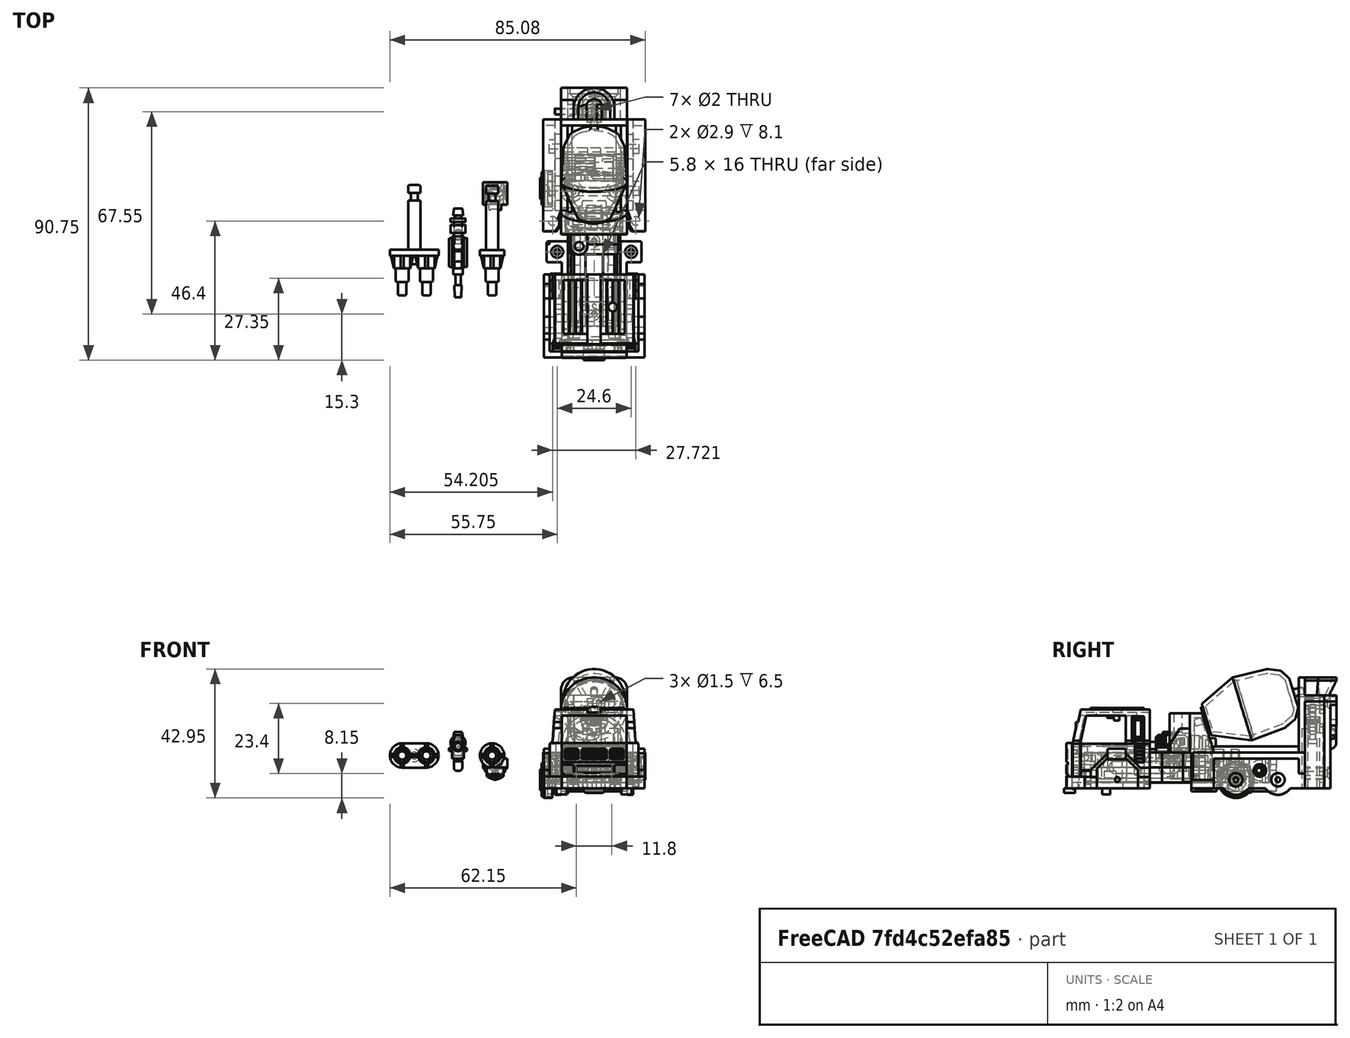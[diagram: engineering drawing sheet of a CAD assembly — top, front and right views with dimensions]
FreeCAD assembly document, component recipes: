
FREECAD ASSEMBLY — COMPONENT RECIPES ("MixMaster")

This assembly document has 25 components, labeled P0..P24 below (a component is one placed body or linked part). 24 of them carry a construction recipe — the FreeCAD feature program that regenerates the part from scratch, quoted from this document or its linked companion documents; the rest are supplied as boundary geometry only. No exploded tour is included for this assembly.
NOTE — document 3 of 4 of this assembly tour. The two overview renders and the header above are repeated from document 1; the component sections below continue where the previous document stopped.
COMPONENT P11 — recipe-attached ("Left_Wheel Holder", modeled in this document).
Construction recipe (the document's own serialized feature program — sketch geometry with constraints, then the solid features built on it; lengths are millimeters unless a unit is written):

FEATURE [PartDesign::SubShapeBinder] Binder013
  BindCopyOnChange = 0
  BindMode = 2
  ClaimChildren = false
  Context = -> Body021 [Binder013.]
  Fuse = false
  MakeFace = true
  OffsetFill = false
  OffsetIntersection = false
  OffsetJoinType = 0
  OffsetOpenResult = false
  PartialLoad = false
  Refine = true
  Relative = true
  _Version = 2
FEATURE [Sketcher::SketchObject] Sketch216
  ArcFitTolerance = 1e-06
  AttachmentSupport = -> [Binder013]
  ExternalGeometry = -> [Binder013]
  FullyConstrained = true
  MakeInternals = false
  MapMode = 5
  Placement = pos=(0.2,0,1.9e-15) rot=(0.57735,-0.57735,-0.57735;2.0944rad)
  sketch-geometry (6):
    g0: LineSegment StartX=77.35 StartY=0.7 StartZ=0 EndX=56.15 EndY=0.7 EndZ=0
    g1: LineSegment StartX=56.15 StartY=0.7 StartZ=0 EndX=56.15 EndY=-11 EndZ=0
    g2: LineSegment StartX=56.15 StartY=-11 StartZ=0 EndX=73.85 EndY=-11 EndZ=0
    g3: LineSegment StartX=73.85 StartY=-11 StartZ=0 EndX=73.85 EndY=-3.1 EndZ=0
    g4: LineSegment StartX=73.85 StartY=-3.1 StartZ=0 EndX=77.35 EndY=-3.1 EndZ=0
    g5: LineSegment StartX=77.35 StartY=-3.1 StartZ=0 EndX=77.35 EndY=0.7 EndZ=0
  constraints (18):
    c: Horizontal(g0)
    c: Coincident(g1,g0)
    c: Vertical(g1)
    c: Coincident(g2,g1)
    c: PointOnObject(g2,g-4)
    c: Horizontal(g2)
    c: Coincident(g3,g2)
    c: Vertical(g3)
    c: Coincident(g4,g3)
    c: Horizontal(g4)
    c: Coincident(g5,g4)
    c: Coincident(g5,g0)
    c: Vertical(g5)
    c: DistanceY(g1,g1) = 11.7
    c: DistanceY(g5,g5) = 3.8
    c: DistanceX(g4,g4) = 3.5
    c: DistanceX(g0,g0) = 21.2
    c: DistanceX(g4,g-4) = 1.7
FEATURE [PartDesign::Pad] Pad154
  Direction = (-1,0,-9.3e-15)
  Length = 2
  Length2 = 10
  Profile = -> Sketch216
  ReferenceAxis = -> Sketch216 [N_Axis]
  Refine = true
  Suppressed = false
  Type = 0
FEATURE [Sketcher::SketchObject] Sketch217
  ArcFitTolerance = 1e-06
  AttachmentSupport = -> [Pad154]
  ExternalGeometry = -> [Pad154]
  FullyConstrained = true
  MakeInternals = false
  MapMode = 5
  Placement = pos=(-1.8,0,-1.68e-14) rot=(0.57735,-0.57735,-0.57735;2.0944rad)
  sketch-geometry (12):
    g0: LineSegment StartX=62.15 StartY=0.7 StartZ=0 EndX=62.15 EndY=-1.3 EndZ=0
    g1: LineSegment StartX=62.15 StartY=-1.3 StartZ=0 EndX=68.25 EndY=-1.3 EndZ=0
    g2: LineSegment StartX=68.25 StartY=-1.3 StartZ=0 EndX=68.25 EndY=0.7 EndZ=0
    g3: LineSegment StartX=68.25 StartY=0.7 StartZ=0 EndX=62.15 EndY=0.7 EndZ=0
    g4: LineSegment StartX=73.85 StartY=-11 StartZ=0 EndX=73.85 EndY=-7.1 EndZ=0
    g5: LineSegment StartX=73.85 StartY=-7.1 StartZ=0 EndX=71.85 EndY=-7.1 EndZ=0
    g6: LineSegment StartX=71.85 StartY=-7.1 StartZ=0 EndX=71.85 EndY=-11 EndZ=0
    g7: LineSegment StartX=71.85 StartY=-11 StartZ=0 EndX=73.85 EndY=-11 EndZ=0
    g8: LineSegment StartX=56.15 StartY=-11 StartZ=0 EndX=58.15 EndY=-11 EndZ=0
    g9: LineSegment StartX=58.15 StartY=-11 StartZ=0 EndX=58.15 EndY=-7.1 EndZ=0
    g10: LineSegment StartX=58.15 StartY=-7.1 StartZ=0 EndX=56.15 EndY=-7.1 EndZ=0
    g11: LineSegment StartX=56.15 StartY=-7.1 StartZ=0 EndX=56.15 EndY=-11 EndZ=0
  constraints (34):
    c: Coincident(g0,g1)
    c: Coincident(g1,g2)
    c: Coincident(g2,g3)
    c: Coincident(g3,g0)
    c: Vertical(g0)
    c: Vertical(g2)
    c: Horizontal(g1)
    c: Horizontal(g3)
    c: PointOnObject(g0,g-5)
    c: Coincident(g4,g5)
    c: Coincident(g5,g6)
    c: Coincident(g6,g7)
    c: Coincident(g7,g4)
    c: Vertical(g4)
    c: Vertical(g6)
    c: Horizontal(g5)
    c: Horizontal(g7)
    c: Coincident(g4,g-6)
    c: Coincident(g8,g9)
    c: Coincident(g9,g10)
    c: Coincident(g10,g11)
    c: Coincident(g11,g8)
    c: Horizontal(g8)
    c: Horizontal(g10)
    c: Vertical(g9)
    c: Vertical(g11)
    c: Coincident(g8,g-6)
    c: DistanceX(g10,g10) = 2
    c: DistanceX(g5,g5) = 2
    c: DistanceY(g2,g2) = 2
    c: DistanceY(g9,g9) = 3.9
    c: DistanceY(g6,g6) = 3.9
    c: DistanceX(g1,g1) = 6.1
    c: DistanceX(g-5,g0) = 6
FEATURE [PartDesign::Pad] Pad155
  BaseFeature = -> Pad154
  Direction = (-1,0,-9.3e-15)
  Length = 2
  Length2 = 10
  Profile = -> Sketch217
  ReferenceAxis = -> Sketch217 [N_Axis]
  Refine = true
  Suppressed = false
  Type = 0
FEATURE [Sketcher::SketchObject] Sketch218
  ArcFitTolerance = 1e-06
  AttachmentSupport = -> [Pad155]
  ExternalGeometry = -> [Pad155]
  FullyConstrained = true
  MakeInternals = false
  MapMode = 5
  Placement = pos=(-3.8,0,-3.54e-14) rot=(0.57735,-0.57735,-0.57735;2.0944rad)
  sketch-geometry (12):
    g0: LineSegment StartX=58.15 StartY=-7.1 StartZ=0 EndX=54.15 EndY=-7.1 EndZ=0
    g1: LineSegment StartX=54.15 StartY=-7.1 StartZ=0 EndX=54.15 EndY=-11 EndZ=0
    g2: LineSegment StartX=54.15 StartY=-11 StartZ=0 EndX=58.15 EndY=-11 EndZ=0
    g3: LineSegment StartX=58.15 StartY=-11 StartZ=0 EndX=58.15 EndY=-7.1 EndZ=0
    g4: LineSegment StartX=71.85 StartY=-7.1 StartZ=0 EndX=71.85 EndY=-11 EndZ=0
    g5: LineSegment StartX=71.85 StartY=-11 StartZ=0 EndX=75.85 EndY=-11 EndZ=0
    g6: LineSegment StartX=75.85 StartY=-11 StartZ=0 EndX=75.85 EndY=-7.1 EndZ=0
    g7: LineSegment StartX=75.85 StartY=-7.1 StartZ=0 EndX=71.85 EndY=-7.1 EndZ=0
    g8: LineSegment StartX=68.25 StartY=-1.3 StartZ=0 EndX=68.25 EndY=2.2 EndZ=0
    g9: LineSegment StartX=68.25 StartY=2.2 StartZ=0 EndX=62.15 EndY=2.2 EndZ=0
    g10: LineSegment StartX=62.15 StartY=2.2 StartZ=0 EndX=62.15 EndY=-1.3 EndZ=0
    g11: LineSegment StartX=62.15 StartY=-1.3 StartZ=0 EndX=68.25 EndY=-1.3 EndZ=0
  constraints (31):
    c: Coincident(g0,g1)
    c: Coincident(g1,g2)
    c: Coincident(g2,g3)
    c: Coincident(g3,g0)
    c: Horizontal(g0)
    c: Horizontal(g2)
    c: Vertical(g1)
    c: Coincident(g0,g-7)
    c: Coincident(g4,g5)
    c: Coincident(g5,g6)
    c: Coincident(g6,g7)
    c: Coincident(g7,g4)
    c: Vertical(g6)
    c: Horizontal(g5)
    c: Horizontal(g7)
    c: Coincident(g4,g-10)
    c: Coincident(g8,g9)
    c: Coincident(g9,g10)
    c: Coincident(g10,g11)
    c: Coincident(g11,g8)
    c: Vertical(g8)
    c: Vertical(g10)
    c: Horizontal(g9)
    c: Horizontal(g11)
    c: Coincident(g8,g-4)
    c: PointOnObject(g-5,g10)
    c: Coincident(g-11,g4)
    c: Coincident(g2,g-8)
    c: DistanceX(g0,g0) = 4
    c: DistanceX(g7,g7) = 4
    c: DistanceY(g8,g8) = 3.5
FEATURE [PartDesign::Pad] Pad156
  BaseFeature = -> Pad155
  Direction = (-1,0,-9.3e-15)
  Length = 2
  Length2 = 10
  Profile = -> Sketch218
  ReferenceAxis = -> Sketch218 [N_Axis]
  Refine = true
  Suppressed = false
  Type = 0
FEATURE [Sketcher::SketchObject] Sketch219
  ArcFitTolerance = 1e-06
  AttachmentSupport = -> [Pad156]
  ExternalGeometry = -> [Pad156]
  FullyConstrained = true
  MakeInternals = false
  MapMode = 5
  Placement = pos=(-1.8,0,-1.68e-14) rot=(0.57735,-0.57735,-0.57735;2.0944rad)
  sketch-geometry (1):
    g0: Circle CenterX=65 CenterY=-8 CenterZ=0 NormalX=0 NormalY=0 NormalZ=1 AngleXU=0 Radius=0.75
  constraints (4):
    c: DistanceX(g-3,g-3) = 13.7
    c: Diameter(g0) = 1.5
    c: DistanceX(g-3,g0) = 6.85
    c: DistanceY(g-3,g0) = 3
FEATURE [PartDesign::Pocket] Pocket206
  BaseFeature = -> Pad156
  Direction = (1,0,9.3e-15)
  Length = 2
  Length2 = 5
  Profile = -> Sketch219
  ReferenceAxis = -> Sketch219 [N_Axis]
  Refine = true
  Suppressed = false
  Type = 0
FEATURE [Sketcher::SketchObject] Sketch220
  ArcFitTolerance = 1e-06
  AttachmentSupport = -> [Pocket206]
  ExternalGeometry = -> [Pocket206]
  FullyConstrained = true
  MakeInternals = false
  MapMode = 5
  Placement = pos=(-3.8,0,-3.54e-14) rot=(0.57735,0.57735,0.57735;2.0944rad)
  sketch-geometry (8):
    g0: LineSegment StartX=-75.85 StartY=-8.55 StartZ=0 EndX=-75.85 EndY=-9.55 EndZ=0
    g1: LineSegment StartX=-75.85 StartY=-9.55 StartZ=0 EndX=-73.85 EndY=-9.55 EndZ=0
    g2: LineSegment StartX=-73.85 StartY=-9.55 StartZ=0 EndX=-73.85 EndY=-8.55 EndZ=0
    g3: LineSegment StartX=-73.85 StartY=-8.55 StartZ=0 EndX=-75.85 EndY=-8.55 EndZ=0
    g4: LineSegment StartX=-54.15 StartY=-8.55 StartZ=0 EndX=-56.15 EndY=-8.55 EndZ=0
    g5: LineSegment StartX=-56.15 StartY=-8.55 StartZ=0 EndX=-56.15 EndY=-9.55 EndZ=0
    g6: LineSegment StartX=-56.15 StartY=-9.55 StartZ=0 EndX=-54.15 EndY=-9.55 EndZ=0
    g7: LineSegment StartX=-54.15 StartY=-9.55 StartZ=0 EndX=-54.15 EndY=-8.55 EndZ=0
  constraints (25):
    c: Coincident(g0,g1)
    c: Coincident(g1,g2)
    c: Coincident(g2,g3)
    c: Coincident(g3,g0)
    c: Vertical(g0)
    c: Vertical(g2)
    c: Horizontal(g1)
    c: Horizontal(g3)
    c: PointOnObject(g0,g-10)
    c: PointOnObject(g1,g-8)
    c: Coincident(g4,g5)
    c: Coincident(g5,g6)
    c: Coincident(g6,g7)
    c: Coincident(g7,g4)
    c: Horizontal(g4)
    c: Horizontal(g6)
    c: Vertical(g5)
    c: Vertical(g7)
    c: PointOnObject(g4,g-4)
    c: PointOnObject(g5,g-3)
    c: DistanceY(g7,g7) = 1
    c: DistanceY(g0,g0) = 1
    c: DistanceY(g-10,g-10) = 3.9
    c: DistanceY(g0,g-10) = 1.45
    c: DistanceY(g4,g-5) = 1.45
FEATURE [PartDesign::Pad] Pad157
  BaseFeature = -> Pocket206
  Direction = (1,0,9.3e-15)
  Length = 0.25
  Length2 = 10
  Profile = -> Sketch220
  ReferenceAxis = -> Sketch220 [N_Axis]
  Refine = true
  Suppressed = false
  Type = 0
FEATURE [PartDesign::Fillet] Fillet014
  Base = -> Pad157 [Edge76,Edge78,Edge85,Edge86]
  BaseFeature = -> Pad157
  Radius = 0.24
  Refine = true
  SupportTransform = false
  Suppressed = false
  UseAllEdges = false
FEATURE [Sketcher::SketchObject] Sketch221
  ArcFitTolerance = 1e-06
  AttachmentSupport = -> [Fillet014]
  ExternalGeometry = -> [Fillet014]
  FullyConstrained = true
  MakeInternals = false
  MapMode = 5
  Placement = pos=(0.2,0,1.9e-15) rot=(0.57735,0.57735,0.57735;2.0944rad)
  sketch-geometry (2):
    g0: Circle CenterX=-58.32 CenterY=-5.4 CenterZ=0 NormalX=0 NormalY=0 NormalZ=1 AngleXU=0 Radius=1.1
    g1: Circle CenterX=-75.55 CenterY=-0.67 CenterZ=0 NormalX=0 NormalY=0 NormalZ=1 AngleXU=0 Radius=1
  constraints (7):
    c: Diameter(g1) = 2
    c: Diameter(g0) = 2.2
    c: DistanceX(g0,g-5) = 2.17
    c: DistanceY(g0,g-4) = 6.1
    c: DistanceX(g-6,g1) = 1.8
    c: DistanceY(g-6,g-6) = 3.8
    c: DistanceY(g1,g-6) = 1.37
FEATURE [PartDesign::Pad] Pad158
  BaseFeature = -> Fillet014
  Direction = (1,0,9.3e-15)
  Length = 2
  Length2 = 10
  Profile = -> Sketch221 [Edge2]
  ReferenceAxis = -> Sketch221 [N_Axis]
  Refine = true
  Suppressed = false
  Type = 0
FEATURE [PartDesign::Pad] Pad159
  BaseFeature = -> Pad158
  Direction = (1,0,9.3e-15)
  Length = 0.95
  Length2 = 10
  Profile = -> Sketch221 [Edge1]
  ReferenceAxis = -> Sketch221 [N_Axis]
  Refine = true
  Suppressed = false
  Type = 0
FEATURE [Sketcher::SketchObject] Sketch251
  ArcFitTolerance = 1e-06
  AttachmentSupport = -> [Pad159]
  ExternalGeometry = -> [Pad159]
  FullyConstrained = true
  MakeInternals = false
  MapMode = 5
  Placement = pos=(-3.55,0,-3.31e-14) rot=(0.57735,0.57735,0.57735;2.0944rad)
  sketch-geometry (8):
    g0: LineSegment StartX=-73.85 StartY=-8.39 StartZ=0 EndX=-75.85 EndY=-8.39 EndZ=0
    g1: LineSegment StartX=-75.85 StartY=-8.39 StartZ=0 EndX=-75.85 EndY=-9.71 EndZ=0
    g2: LineSegment StartX=-75.85 StartY=-9.71 StartZ=0 EndX=-73.85 EndY=-9.71 EndZ=0
    g3: LineSegment StartX=-73.85 StartY=-9.71 StartZ=0 EndX=-73.85 EndY=-8.39 EndZ=0
    g4: LineSegment StartX=-56.15 StartY=-8.39 StartZ=0 EndX=-56.15 EndY=-9.71 EndZ=0
    g5: LineSegment StartX=-56.15 StartY=-9.71 StartZ=0 EndX=-54.15 EndY=-9.71 EndZ=0
    g6: LineSegment StartX=-54.15 StartY=-9.71 StartZ=0 EndX=-54.15 EndY=-8.39 EndZ=0
    g7: LineSegment StartX=-54.15 StartY=-8.39 StartZ=0 EndX=-56.15 EndY=-8.39 EndZ=0
  constraints (24):
    c: Coincident(g0,g1)
    c: Coincident(g1,g2)
    c: Coincident(g2,g3)
    c: Coincident(g3,g0)
    c: Horizontal(g0)
    c: Horizontal(g2)
    c: Vertical(g1)
    c: Vertical(g3)
    c: PointOnObject(g-8,g3)
    c: PointOnObject(g-10,g1)
    c: DistanceY(g-10,g0) = 0.4
    c: DistanceY(g1,g-10) = 0.4
    c: Coincident(g4,g5)
    c: Coincident(g5,g6)
    c: Coincident(g6,g7)
    c: Coincident(g7,g4)
    c: Vertical(g4)
    c: Vertical(g6)
    c: Horizontal(g5)
    c: Horizontal(g7)
    c: PointOnObject(g-4,g4)
    c: PointOnObject(g-6,g6)
    c: DistanceY(g-6,g6) = 0.4
    c: DistanceY(g5,g-6) = 0.4
FEATURE [PartDesign::Pocket] Pocket082
  BaseFeature = -> Pad159
  Direction = (-1,0,-9.3e-15)
  Length = 0.1
  Length2 = 5
  Profile = -> Sketch251
  ReferenceAxis = -> Sketch251 [N_Axis]
  Refine = true
  Suppressed = false
  Type = 0
FEATURE [Sketcher::SketchObject] Sketch252
  ArcFitTolerance = 1e-06
  AttachmentSupport = -> [Pocket082]
  ExternalGeometry = -> [Pocket082]
  FullyConstrained = true
  MakeInternals = false
  MapMode = 5
  Placement = pos=(0.2,0,1.9e-15) rot=(0.57735,0.57735,0.57735;2.0944rad)
  sketch-geometry (6):
    g0: LineSegment StartX=-73.85 StartY=-3.1 StartZ=0 EndX=-71.35 EndY=-3.1 EndZ=0
    g1: LineSegment StartX=-70.35 StartY=-2.1 StartZ=0 EndX=-70.35 EndY=0.7 EndZ=0
    g2: LineSegment StartX=-70.35 StartY=0.7 StartZ=0 EndX=-73.85 EndY=0.7 EndZ=0
    g3: LineSegment StartX=-73.85 StartY=0.7 StartZ=0 EndX=-73.85 EndY=-3.1 EndZ=0
    g4: ArcOfCircle CenterX=-71.35 CenterY=-2.1 CenterZ=0 NormalX=0 NormalY=0 NormalZ=1 AngleXU=0 Radius=1 StartAngle=4.71239 EndAngle=6.28319
    g5: GeomPoint [constr] X=-70.35 Y=-3.1 Z=0
  constraints (15):
    c: Coincident(g1,g2)
    c: Coincident(g2,g3)
    c: Coincident(g3,g0)
    c: Horizontal(g0)
    c: Horizontal(g2)
    c: Vertical(g1)
    c: Vertical(g3)
    c: Coincident(g0,g-4)
    c: PointOnObject(g1,g-3)
    c: PointOnObject(g5,g0)
    c: PointOnObject(g5,g1)
    c: Tangent(g0,g4) = -1.5708
    c: Tangent(g1,g4) = -1.5708
    c: DistanceX(g2,g2) = 3.5
    c: Radius(g4) = 1
FEATURE [PartDesign::Pad] Pad171
  BaseFeature = -> Pocket082
  Direction = (1,0,9.3e-15)
  Length = 0.25
  Length2 = 10
  Profile = -> Sketch252
  ReferenceAxis = -> Sketch252 [N_Axis]
  Refine = true
  Suppressed = false
  Type = 0
FEATURE [Sketcher::SketchObject] Sketch312
  ArcFitTolerance = 1e-06
  AttachmentSupport = -> [Pad171]
  ExternalGeometry = -> [Pad171]
  FullyConstrained = true
  MakeInternals = false
  MapMode = 5
  Placement = pos=(-1.8,0,-1.68e-14) rot=(0.57735,-0.57735,-0.57735;2.0944rad)
  sketch-geometry (1):
    g0: Circle CenterX=65 CenterY=-8 CenterZ=0 NormalX=0 NormalY=0 NormalZ=1 AngleXU=0 Radius=0.8
  constraints (2):
    c: Coincident(g0,g-3)
    c: Radius(g0) = 0.8
FEATURE [PartDesign::Pocket] Pocket220
  BaseFeature = -> Pad171
  Direction = (1,0,9.3e-15)
  Length = 5
  Length2 = 5
  Profile = -> Sketch312
  ReferenceAxis = -> Sketch312 [N_Axis]
  Refine = true
  Suppressed = false
  Type = 0
FEATURE [PartDesign::Pad] Pad215
  BaseFeature = -> Pocket220
  Direction = (1,0,9.3e-15)
  Length = 0.05
  Length2 = 10
  Profile = -> Pocket220 [Face41]
  Refine = true
  Suppressed = false
  Type = 0
FEATURE [PartDesign::Body] Body021  label="Left_Wheel Holder"
  AllowCompound = false
  Group = -> [Binder013,Sketch216,Pad154,Sketch217,Pad155,Sketch218,Pad156,Sketch219,Pocket206,Sketch220,Pad157,Fillet014,Sketch221,Pad158,Pad159,Sketch251,Pocket082,Sketch252,Pad171,Sketch312,Pocket220,Pad215]
  Origin = -> Origin023
  Placement = pos=(33,38,0) rot=(0,0,1;0rad)
  Tip = -> Pad215
COMPONENT P12 — recipe-attached ("Cab", modeled in this document).
Construction recipe (the document's own serialized feature program — sketch geometry with constraints, then the solid features built on it; lengths are millimeters unless a unit is written):

FEATURE [PartDesign::SubShapeBinder] Binder014
  BindCopyOnChange = 0
  BindMode = 2
  ClaimChildren = false
  Context = -> Body022 [Binder014.]
  Fuse = false
  MakeFace = true
  OffsetFill = false
  OffsetIntersection = false
  OffsetJoinType = 0
  OffsetOpenResult = false
  PartialLoad = false
  Refine = true
  Relative = true
  _Version = 2
FEATURE [Sketcher::SketchObject] Sketch222
  ArcFitTolerance = 1e-06
  AttachmentSupport = -> [Binder014]
  ExternalGeometry = -> [Binder014]
  FullyConstrained = true
  MakeInternals = false
  MapMode = 5
  Placement = pos=(-3.8,0,-3.54e-14) rot=(0.57735,0.57735,0.57735;2.0944rad)
  sketch-geometry (22):
    g0: LineSegment StartX=-62.15 StartY=0.7 StartZ=0 EndX=-68.25 EndY=0.7 EndZ=0
    g1: LineSegment StartX=-68.25 StartY=0.7 StartZ=0 EndX=-68.25 EndY=-0.9 EndZ=0
    g2: LineSegment StartX=-68.25 StartY=-0.9 StartZ=0 EndX=-71.85 EndY=-4.5 EndZ=0
    g3: LineSegment StartX=-71.85 StartY=-4.5 StartZ=0 EndX=-71.85 EndY=-7.1 EndZ=0
    g4: LineSegment StartX=-71.85 StartY=-7.1 StartZ=0 EndX=-73.85 EndY=-7.1 EndZ=0
    g5: LineSegment StartX=-73.85 StartY=-7.1 StartZ=0 EndX=-73.85 EndY=-11 EndZ=0
    g6: LineSegment StartX=-73.85 StartY=-11 StartZ=0 EndX=-81.85 EndY=-11 EndZ=0
    g7: LineSegment StartX=-81.85 StartY=-11 StartZ=0 EndX=-81.85 EndY=-7 EndZ=0
    g8: LineSegment StartX=-81.85 StartY=-7 StartZ=0 EndX=-79.85 EndY=-7 EndZ=0
    g9: LineSegment StartX=-79.85 StartY=-7 StartZ=0 EndX=-79.85 EndY=4.2 EndZ=0
    g10: LineSegment StartX=-79.85 StartY=4.2 StartZ=0 EndX=-78.8 EndY=9.1 EndZ=0
    g11: LineSegment StartX=-78.8 StartY=9.1 StartZ=0 EndX=-78.8 EndY=11.1 EndZ=0
    g12: LineSegment StartX=-78.8 StartY=11.1 StartZ=0 EndX=-78.05 EndY=11.1 EndZ=0
    g13: LineSegment StartX=-78.05 StartY=11.1 StartZ=0 EndX=-77.15 EndY=15.3 EndZ=0
    g14: LineSegment StartX=-77.15 StartY=15.3 StartZ=0 EndX=-54.15 EndY=15.3 EndZ=0
    g15: LineSegment StartX=-54.15 StartY=15.3 StartZ=0 EndX=-54.15 EndY=-11 EndZ=0
    g16: LineSegment StartX=-54.15 StartY=-11 StartZ=0 EndX=-56.15 EndY=-11 EndZ=0
    g17: LineSegment StartX=-56.15 StartY=-11 StartZ=0 EndX=-56.15 EndY=-7.1 EndZ=0
    g18: LineSegment StartX=-56.15 StartY=-7.1 StartZ=0 EndX=-58.15 EndY=-7.1 EndZ=0
    g19: LineSegment StartX=-58.15 StartY=-7.1 StartZ=0 EndX=-58.15 EndY=-4.9 EndZ=0
    g20: LineSegment StartX=-58.15 StartY=-4.9 StartZ=0 EndX=-62.15 EndY=-0.9 EndZ=0
    g21: LineSegment StartX=-62.15 StartY=-0.9 StartZ=0 EndX=-62.15 EndY=0.7 EndZ=0
  constraints (60):
    c: Coincident(g0,g-3)
    c: Coincident(g0,g-3)
    c: Coincident(g1,g0)
    c: Vertical(g1)
    c: Coincident(g2,g1)
    c: Coincident(g3,g2)
    c: Vertical(g3)
    c: Coincident(g4,g3)
    c: Coincident(g4,g-4)
    c: Coincident(g5,g4)
    c: Coincident(g5,g-6)
    c: Coincident(g6,g5)
    c: Horizontal(g6)
    c: Coincident(g7,g6)
    c: Vertical(g7)
    c: Coincident(g8,g7)
    c: Horizontal(g8)
    c: Coincident(g9,g8)
    c: Vertical(g9)
    c: Coincident(g10,g9)
    c: Coincident(g11,g10)
    c: Vertical(g11)
    c: Horizontal(g12)
    c: Coincident(g13,g12)
    c: Coincident(g14,g13)
    c: Horizontal(g14)
    c: Coincident(g15,g14)
    c: Vertical(g15)
    c: Coincident(g16,g15)
    c: Coincident(g16,g-9)
    c: Coincident(g17,g16)
    c: Coincident(g17,g-7)
    c: Coincident(g18,g17)
    c: Horizontal(g18)
    c: Coincident(g19,g18)
    c: Vertical(g19)
    c: Coincident(g20,g19)
    c: Coincident(g21,g20)
    c: Coincident(g21,g0)
    c: DistanceY(g15,g15) = 26.3
    c: Coincident(g12,g11)
    c: Horizontal(g16)
    c: Horizontal(g4)
    c: Vertical(g21)
    c: DistanceY(g1,g1) = 1.6
    c: DistanceY(g21,g21) = 1.6
    c: DistanceX(g6,g6) = 8
    c: DistanceY(g7,g7) = 4
    c: DistanceX(g8,g8) = 2
    c: DistanceY(g6,g9) = 15.2
    c: DistanceX(g14,g14) = 23
    c: DistanceX(g16,g16) = 2
    c: Angle(g20,g-1) = 0.785398
    c: Angle(g2,g-1) = 2.35619
    c: Parallel(g13,g10)
    c: DistanceX(g12,g12) = 0.75
    c: DistanceY(g12,g13) = 4.2
    c: DistanceY(g11,g11) = 2
    c: DistanceX(g4,g4) = 2
    c: DistanceX(g18,g18) = 2
FEATURE [PartDesign::Pad] Pad160
  Direction = (1,0,9.3e-15)
  Length = 2
  Length2 = 10
  Profile = -> Sketch222
  ReferenceAxis = -> Sketch222 [N_Axis]
  Refine = true
  Suppressed = false
  Type = 0
FEATURE [Sketcher::SketchObject] Sketch223
  ArcFitTolerance = 1e-06
  AttachmentSupport = -> [Pad160]
  ExternalGeometry = -> [Pad160]
  FullyConstrained = true
  MakeInternals = false
  MapMode = 5
  Placement = pos=(-3.8,0,-3.54e-14) rot=(0.57735,-0.57735,-0.57735;2.0944rad)
  sketch-geometry (17):
    g0: LineSegment StartX=62.15 StartY=0.7 StartZ=0 EndX=62.15 EndY=-0.9 EndZ=0
    g1: LineSegment StartX=62.15 StartY=-0.9 StartZ=0 EndX=58.15 EndY=-4.9 EndZ=0
    g2: LineSegment StartX=58.15 StartY=-4.9 StartZ=0 EndX=58.15 EndY=-7.1 EndZ=0
    g3: LineSegment StartX=58.15 StartY=-7.1 StartZ=0 EndX=54.15 EndY=-7.1 EndZ=0
    g4: LineSegment StartX=54.15 StartY=-7.1 StartZ=0 EndX=54.15 EndY=-4.1 EndZ=0
    g5: LineSegment StartX=62.15 StartY=0.7 StartZ=0 EndX=57.35 EndY=-4.1 EndZ=0
    g6: LineSegment StartX=57.35 StartY=-4.1 StartZ=0 EndX=54.15 EndY=-4.1 EndZ=0
    g7: LineSegment StartX=68.25 StartY=0.7 StartZ=0 EndX=68.25 EndY=-0.9 EndZ=0
    g8: LineSegment StartX=68.25 StartY=-0.9 StartZ=0 EndX=71.85 EndY=-4.5 EndZ=0
    g9: LineSegment StartX=71.85 StartY=-4.5 StartZ=0 EndX=71.85 EndY=-7.1 EndZ=0
    g10: LineSegment StartX=71.85 StartY=-7.1 StartZ=0 EndX=73.85 EndY=-7.1 EndZ=0
    g11: LineSegment StartX=73.85 StartY=-7.1 StartZ=0 EndX=73.85 EndY=-4.9 EndZ=0
    g12: LineSegment StartX=68.25 StartY=0.7 StartZ=0 EndX=73.85 EndY=-4.9 EndZ=0
    g13: LineSegment StartX=81.85 StartY=-7 StartZ=0 EndX=75.85 EndY=-7 EndZ=0
    g14: LineSegment StartX=75.85 StartY=-7 StartZ=0 EndX=75.85 EndY=-11 EndZ=0
    g15: LineSegment StartX=75.85 StartY=-11 StartZ=0 EndX=81.85 EndY=-11 EndZ=0
    g16: LineSegment StartX=81.85 StartY=-11 StartZ=0 EndX=81.85 EndY=-7 EndZ=0
  constraints (41):
    c: Coincident(g0,g-10)
    c: Coincident(g0,g-11)
    c: Coincident(g1,g0)
    c: Coincident(g1,g-12)
    c: Coincident(g2,g1)
    c: Coincident(g2,g-13)
    c: Coincident(g3,g2)
    c: PointOnObject(g3,g-14)
    c: Horizontal(g3)
    c: Coincident(g4,g3)
    c: PointOnObject(g4,g-14)
    c: Coincident(g5,g0)
    c: Coincident(g6,g5)
    c: Coincident(g6,g4)
    c: Horizontal(g6)
    c: Parallel(g5,g1)
    c: DistanceY(g4,g4) = 3
    c: Coincident(g7,g-8)
    c: Coincident(g7,g-8)
    c: Coincident(g8,g7)
    c: Coincident(g8,g-7)
    c: Coincident(g9,g8)
    c: Coincident(g9,g-6)
    c: Coincident(g10,g9)
    c: Coincident(g10,g-15)
    c: Coincident(g11,g10)
    c: Vertical(g11)
    c: Coincident(g12,g7)
    c: Coincident(g12,g11)
    c: Parallel(g12,g8)
    c: Coincident(g13,g14)
    c: Coincident(g14,g15)
    c: Coincident(g15,g16)
    c: Coincident(g16,g13)
    c: Horizontal(g13)
    c: Horizontal(g15)
    c: Vertical(g14)
    c: Vertical(g16)
    c: Coincident(g13,g-4)
    c: PointOnObject(g14,g-5)
    c: DistanceX(g-5,g14) = 2
FEATURE [PartDesign::Pad] Pad161
  BaseFeature = -> Pad160
  Direction = (-1,0,-9.3e-15)
  Length = 2
  Length2 = 10
  Profile = -> Sketch223
  ReferenceAxis = -> Sketch223 [N_Axis]
  Refine = true
  Suppressed = false
  Type = 0
FEATURE [Sketcher::SketchObject] Sketch224
  ArcFitTolerance = 1e-06
  AttachmentSupport = -> [Pad161]
  ExternalGeometry = -> [Pad161]
  FullyConstrained = true
  MakeInternals = false
  MapMode = 5
  Placement = pos=(-3.8,0,-3.54e-14) rot=(0.57735,-0.57735,-0.57735;2.0944rad)
  sketch-geometry (8):
    g0: LineSegment StartX=56.15 StartY=-8.55 StartZ=0 EndX=54.15 EndY=-8.55 EndZ=0
    g1: LineSegment StartX=54.15 StartY=-8.55 StartZ=0 EndX=54.15 EndY=-9.55 EndZ=0
    g2: LineSegment StartX=54.15 StartY=-9.55 StartZ=0 EndX=56.15 EndY=-9.55 EndZ=0
    g3: LineSegment StartX=56.15 StartY=-9.55 StartZ=0 EndX=56.15 EndY=-8.55 EndZ=0
    g4: LineSegment StartX=73.85 StartY=-8.55 StartZ=0 EndX=73.85 EndY=-9.55 EndZ=0
    g5: LineSegment StartX=73.85 StartY=-9.55 StartZ=0 EndX=75.85 EndY=-9.55 EndZ=0
    g6: LineSegment StartX=75.85 StartY=-9.55 StartZ=0 EndX=75.85 EndY=-8.55 EndZ=0
    g7: LineSegment StartX=75.85 StartY=-8.55 StartZ=0 EndX=73.85 EndY=-8.55 EndZ=0
  constraints (25):
    c: DistanceY(g-3,g-3) = 3.9
    c: Coincident(g0,g1)
    c: Coincident(g1,g2)
    c: Coincident(g2,g3)
    c: Coincident(g3,g0)
    c: Horizontal(g0)
    c: Horizontal(g2)
    c: Vertical(g1)
    c: Vertical(g3)
    c: PointOnObject(g0,g-3)
    c: PointOnObject(g1,g-4)
    c: Coincident(g4,g5)
    c: Coincident(g5,g6)
    c: Coincident(g6,g7)
    c: Coincident(g7,g4)
    c: Vertical(g4)
    c: Vertical(g6)
    c: Horizontal(g5)
    c: Horizontal(g7)
    c: PointOnObject(g5,g-6)
    c: DistanceY(g3,g3) = 1
    c: DistanceY(g4,g4) = 1
    c: DistanceY(g-4,g1) = 1.45
    c: DistanceY(g-5,g4) = 1.45
    c: PointOnObject(g4,g-5)
FEATURE [PartDesign::Pocket] Pocket064
  BaseFeature = -> Pad161
  Direction = (1,0,9.3e-15)
  Length = 0.25
  Length2 = 5
  Profile = -> Sketch224
  ReferenceAxis = -> Sketch224 [N_Axis]
  Refine = true
  Suppressed = false
  Type = 0
FEATURE [PartDesign::Fillet] Fillet015
  Base = -> Pocket064 [Edge16,Edge108,Edge111,Edge114]
  BaseFeature = -> Pocket064
  Radius = 0.1
  Refine = true
  SupportTransform = false
  Suppressed = false
  UseAllEdges = false
FEATURE [Sketcher::SketchObject] Sketch225
  ArcFitTolerance = 1e-06
  AttachmentSupport = -> [Fillet015]
  ExternalGeometry = -> [Fillet015]
  FullyConstrained = true
  MakeInternals = false
  MapMode = 5
  Placement = pos=(-3.8,0,-3.54e-14) rot=(0.57735,-0.57735,-0.57735;2.0944rad)
  sketch-geometry (4):
    g0: LineSegment StartX=77.35 StartY=3.9 StartZ=0 EndX=75.3357 EndY=13.3 EndZ=0
    g1: LineSegment StartX=75.3357 StartY=13.3 StartZ=0 EndX=62.15 EndY=13.3 EndZ=0
    g2: LineSegment StartX=62.15 StartY=13.3 StartZ=0 EndX=62.15 EndY=3.9 EndZ=0
    g3: LineSegment StartX=62.15 StartY=3.9 StartZ=0 EndX=77.35 EndY=3.9 EndZ=0
  constraints (12):
    c: Coincident(g1,g0)
    c: Horizontal(g1)
    c: Coincident(g2,g1)
    c: Vertical(g2)
    c: Coincident(g3,g2)
    c: Coincident(g3,g0)
    c: Horizontal(g3)
    c: DistanceX(g-6,g1) = 8
    c: DistanceY(g0,g-5) = 2
    c: DistanceY(g-7,g2) = 3.2
    c: DistanceX(g3,g3) = 15.2
    c: Parallel(g0,g-5)
FEATURE [PartDesign::Pocket] Pocket199
  BaseFeature = -> Fillet015
  Direction = (1,0,9.3e-15)
  Length = 5
  Length2 = 5
  Profile = -> Sketch225
  ReferenceAxis = -> Sketch225 [N_Axis]
  Refine = true
  Suppressed = false
  Type = 0
FEATURE [Sketcher::SketchObject] Sketch226
  ArcFitTolerance = 1e-06
  AttachmentSupport = -> [Pocket199]
  ExternalGeometry = -> [Pocket199]
  FullyConstrained = true
  MakeInternals = false
  MapMode = 5
  Placement = pos=(-2.92e-14,-54.15,0) rot=(0,0.707107,0.707107;3.14159rad)
  sketch-geometry (4):
    g0: LineSegment StartX=3.8 StartY=15.3 StartZ=0 EndX=3.8 EndY=3.9 EndZ=0
    g1: LineSegment StartX=3.8 StartY=15.3 StartZ=0 EndX=2.1 EndY=15.3 EndZ=0
    g2: LineSegment StartX=3.8 StartY=3.9 StartZ=0 EndX=2.8 EndY=4.9 EndZ=0
    g3: LineSegment StartX=2.8 StartY=4.9 StartZ=0 EndX=2.1 EndY=15.3 EndZ=0
  constraints (12):
    c: Coincident(g0,g-3)
    c: PointOnObject(g0,g-3)
    c: Coincident(g1,g0)
    c: DistanceY(g-4,g-4) = 0
    c: PointOnObject(g1,g-4)
    c: DistanceX(g1,g1) = 1.7
    c: DistanceY(g0,g0) = 11.4
    c: Coincident(g2,g0)
    c: Coincident(g3,g2)
    c: Coincident(g3,g1)
    c: DistanceY(g0,g2) = 1
    c: DistanceX(g2,g0) = 1
FEATURE [PartDesign::Pocket] Pocket200
  BaseFeature = -> Pocket199
  Direction = (0,-1,2e-16)
  Length = 27
  Length2 = 5
  Profile = -> Sketch226
  ReferenceAxis = -> Sketch226 [N_Axis]
  Refine = true
  Suppressed = false
  Type = 0
FEATURE [Sketcher::SketchObject] Sketch227
  ArcFitTolerance = 1e-06
  AttachmentSupport = -> [Pocket200]
  ExternalGeometry = -> [Pocket200]
  FullyConstrained = true
  MakeInternals = false
  MapMode = 5
  Placement = pos=(-1.8,0,-1.68e-14) rot=(0.57735,0.57735,0.57735;2.0944rad)
  sketch-geometry (15):
    g0: LineSegment StartX=-79.85 StartY=-7 StartZ=0 EndX=-81.85 EndY=-7 EndZ=0
    g1: LineSegment StartX=-81.85 StartY=-7 StartZ=0 EndX=-81.85 EndY=-11 EndZ=0
    g2: LineSegment StartX=-81.85 StartY=-11 StartZ=0 EndX=-77.85 EndY=-11 EndZ=0
    g3: LineSegment StartX=-79.85 StartY=-7 StartZ=0 EndX=-79.85 EndY=4.2 EndZ=0
    g4: LineSegment StartX=-79.85 StartY=4.2 StartZ=0 EndX=-78.8 EndY=9.1 EndZ=0
    g5: LineSegment StartX=-78.8 StartY=9.1 StartZ=0 EndX=-78.8 EndY=11.1 EndZ=0
    g6: LineSegment StartX=-78.8 StartY=11.1 StartZ=0 EndX=-78.05 EndY=11.1 EndZ=0
    g7: LineSegment StartX=-78.05 StartY=11.1 StartZ=0 EndX=-77.15 EndY=15.3 EndZ=0
    g8: LineSegment StartX=-77.15 StartY=15.3 StartZ=0 EndX=-75.4714 EndY=15.3 EndZ=0
    g9: LineSegment StartX=-75.4714 StartY=15.3 StartZ=0 EndX=-77.85 EndY=4.2 EndZ=0
    g10: LineSegment StartX=-77.85 StartY=4.2 StartZ=0 EndX=-77.85 EndY=-11 EndZ=0
    g11: LineSegment StartX=-56.15 StartY=-11 StartZ=0 EndX=-54.15 EndY=-11 EndZ=0
    g12: LineSegment StartX=-54.15 StartY=-11 StartZ=0 EndX=-54.15 EndY=15.3 EndZ=0
    g13: LineSegment StartX=-54.15 StartY=15.3 StartZ=0 EndX=-56.15 EndY=15.3 EndZ=0
    g14: LineSegment StartX=-56.15 StartY=15.3 StartZ=0 EndX=-56.15 EndY=-11 EndZ=0
  constraints (34):
    c: Coincident(g0,g-7)
    c: Coincident(g0,g-8)
    c: Coincident(g1,g0)
    c: Coincident(g1,g-9)
    c: Coincident(g2,g1)
    c: Coincident(g3,g0)
    c: Coincident(g3,g-10)
    c: Coincident(g4,g3)
    c: Coincident(g4,g-11)
    c: Coincident(g5,g4)
    c: Coincident(g5,g-11)
    c: Coincident(g6,g5)
    c: Coincident(g6,g-13)
    c: Coincident(g7,g6)
    c: Coincident(g7,g-13)
    c: Coincident(g8,g7)
    c: PointOnObject(g8,g-4)
    c: Coincident(g9,g8)
    c: Coincident(g10,g9)
    c: Coincident(g10,g2)
    c: Vertical(g10)
    c: Coincident(g11,g-6)
    c: Coincident(g11,g-5)
    c: Coincident(g12,g11)
    c: Coincident(g12,g-4)
    c: Coincident(g13,g12)
    c: PointOnObject(g13,g-4)
    c: Coincident(g14,g13)
    c: Coincident(g14,g11)
    c: Vertical(g14)
    c: DistanceX(g3,g9) = 2
    c: PointOnObject(g2,g-9)
    c: DistanceY(g9,g3) = 0
    c: Parallel(g7,g9)
FEATURE [PartDesign::Pad] Pad162
  BaseFeature = -> Pocket200
  Direction = (1,0,9.3e-15)
  Length = 2
  Length2 = 10
  Profile = -> Sketch227
  ReferenceAxis = -> Sketch227 [N_Axis]
  Refine = true
  Suppressed = false
  Type = 0
FEATURE [Sketcher::SketchObject] Sketch228
  ArcFitTolerance = 1e-06
  AttachmentSupport = -> [Pad162]
  ExternalGeometry = -> [Pad162]
  FullyConstrained = true
  MakeInternals = false
  MapMode = 5
  Placement = pos=(3.54e-14,-56.15,0) rot=(1,0,0;1.5708rad)
  sketch-geometry (4):
    g0: LineSegment StartX=-1.8 StartY=3.9 StartZ=0 EndX=-0.8 EndY=4.9 EndZ=0
    g1: LineSegment StartX=-0.8 StartY=4.9 StartZ=0 EndX=0 EndY=15.3 EndZ=0
    g2: LineSegment StartX=0 StartY=15.3 StartZ=0 EndX=-1.8 EndY=15.3 EndZ=0
    g3: LineSegment StartX=-1.8 StartY=15.3 StartZ=0 EndX=-1.8 EndY=3.9 EndZ=0
  constraints (10):
    c: Coincident(g0,g-6)
    c: Coincident(g1,g0)
    c: PointOnObject(g1,g-2)
    c: Coincident(g2,g1)
    c: Coincident(g2,g-4)
    c: Horizontal(g2)
    c: Coincident(g3,g2)
    c: Coincident(g3,g0)
    c: DistanceX(g0,g0) = 1
    c: DistanceY(g0,g0) = 1
FEATURE [PartDesign::Pad] Pad163
  BaseFeature = -> Pad162
  Direction = (0,-1,2e-16)
  Length = 22
  Length2 = 10
  Profile = -> Sketch228
  ReferenceAxis = -> Sketch228 [N_Axis]
  Refine = true
  Suppressed = false
  Type = 0
FEATURE [Sketcher::SketchObject] Sketch229
  ArcFitTolerance = 1e-06
  AttachmentSupport = -> [Pad163]
  ExternalGeometry = -> [Pad163]
  FullyConstrained = true
  MakeInternals = false
  MapMode = 5
  Placement = pos=(-2.029e-13,-76.8976,16.478) rot=(1,0,0;1.3597rad)
  sketch-geometry (4):
    g0: LineSegment StartX=-2.1 StartY=-1.20479 StartZ=0 EndX=-2.1 EndY=-5.50014 EndZ=0
    g1: LineSegment StartX=-2.1 StartY=-5.50014 StartZ=0 EndX=0.2 EndY=-5.50014 EndZ=0
    g2: LineSegment StartX=0.2 StartY=-5.50014 StartZ=0 EndX=0.2 EndY=-1.20479 EndZ=0
    g3: LineSegment StartX=0.2 StartY=-1.20479 StartZ=0 EndX=-2.1 EndY=-1.20479 EndZ=0
  constraints (10):
    c: Coincident(g0,g1)
    c: Coincident(g1,g2)
    c: Coincident(g2,g3)
    c: Coincident(g3,g0)
    c: Vertical(g0)
    c: Vertical(g2)
    c: Horizontal(g1)
    c: Horizontal(g3)
    c: Coincident(g0,g-4)
    c: Coincident(g1,g-7)
FEATURE [PartDesign::Pocket] Pocket201
  BaseFeature = -> Pad163
  Direction = (2.3e-15,0.977802,-0.209529)
  Length = 5
  Length2 = 5
  Profile = -> Sketch229
  ReferenceAxis = -> Sketch229 [N_Axis]
  Refine = true
  Reversed = true
  Suppressed = false
  Type = 0
FEATURE [Sketcher::SketchObject] Sketch230
  ArcFitTolerance = 1e-06
  AttachmentSupport = -> [Pocket201]
  ExternalGeometry = -> [Pocket201]
  FullyConstrained = true
  MakeInternals = false
  MapMode = 5
  Placement = pos=(-3.49e-14,-5.137e-13,11.1) rot=(0,0,1;0rad)
  sketch-geometry (4):
    g0: LineSegment StartX=-2.38269 StartY=-78.05 StartZ=0 EndX=-2.38269 EndY=-78.8 EndZ=0
    g1: LineSegment StartX=-2.38269 StartY=-78.8 StartZ=0 EndX=0.2 EndY=-78.8 EndZ=0
    g2: LineSegment StartX=0.2 StartY=-78.8 StartZ=0 EndX=0.2 EndY=-78.05 EndZ=0
    g3: LineSegment StartX=0.2 StartY=-78.05 StartZ=0 EndX=-2.38269 EndY=-78.05 EndZ=0
  constraints (10):
    c: Coincident(g0,g1)
    c: Coincident(g1,g2)
    c: Coincident(g2,g3)
    c: Coincident(g3,g0)
    c: Vertical(g0)
    c: Vertical(g2)
    c: Horizontal(g1)
    c: Horizontal(g3)
    c: Coincident(g0,g-3)
    c: Coincident(g1,g-4)
FEATURE [PartDesign::Pocket] Pocket202
  BaseFeature = -> Pocket201
  Direction = (3.1e-15,4.63e-14,-1)
  Length = 5
  Length2 = 5
  Profile = -> Sketch230
  ReferenceAxis = -> Sketch230 [N_Axis]
  Refine = true
  Reversed = true
  Suppressed = false
  Type = 0
FEATURE [Sketcher::SketchObject] Sketch231
  ArcFitTolerance = 1e-06
  AttachmentSupport = -> [Pocket202]
  ExternalGeometry = -> [Pocket202]
  FullyConstrained = true
  MakeInternals = false
  MapMode = 5
  Placement = pos=(-1.8,0,1.34e-14) rot=(0.57735,-0.57735,-0.57735;2.0944rad)
  sketch-geometry (4):
    g0: LineSegment StartX=62.15 StartY=13.3 StartZ=0 EndX=62.15 EndY=3.9 EndZ=0
    g1: LineSegment StartX=62.15 StartY=3.9 StartZ=0 EndX=77.35 EndY=3.9 EndZ=0
    g2: LineSegment StartX=77.35 StartY=3.9 StartZ=0 EndX=75.3357 EndY=13.3 EndZ=0
    g3: LineSegment StartX=75.3357 StartY=13.3 StartZ=0 EndX=62.15 EndY=13.3 EndZ=0
  constraints (10):
    c: PointOnObject(g0,g-4)
    c: Coincident(g0,g-6)
    c: Vertical(g0)
    c: Coincident(g1,g0)
    c: Coincident(g1,g-6)
    c: Coincident(g2,g-5)
    c: Coincident(g3,g2)
    c: PointOnObject(g3,g0)
    c: Horizontal(g3)
    c: Coincident(g2,g1)
FEATURE [PartDesign::Pocket] Pocket203
  BaseFeature = -> Pocket202
  Direction = (1,-1e-16,-7.2e-15)
  Length = 5
  Length2 = 5
  Profile = -> Sketch231
  ReferenceAxis = -> Sketch231 [N_Axis]
  Refine = true
  Suppressed = false
  Type = 0
FEATURE [Sketcher::SketchObject] Sketch232
  ArcFitTolerance = 1e-06
  AttachmentSupport = -> [Pocket203]
  ExternalGeometry = -> [Pocket203]
  FullyConstrained = false
  MakeInternals = false
  MapMode = 5
  Placement = pos=(-4.53e-14,0,15.3) rot=(0,0,1;0rad)
  sketch-geometry (4):
    g0: LineSegment StartX=0.2 StartY=-77.15 StartZ=0 EndX=0.2 EndY=-54.15 EndZ=0
    g1: LineSegment StartX=0.2 StartY=-54.15 StartZ=0 EndX=-1.12624 EndY=-54.15 EndZ=0
    g2: LineSegment StartX=-1.12624 StartY=-54.15 StartZ=0 EndX=-1.12624 EndY=-77.15 EndZ=0
    g3: LineSegment StartX=-1.12624 StartY=-77.15 StartZ=0 EndX=0.2 EndY=-77.15 EndZ=0
  constraints (10):
    c: Coincident(g0,g1)
    c: Coincident(g1,g2)
    c: Coincident(g2,g3)
    c: Coincident(g3,g0)
    c: Vertical(g0)
    c: Vertical(g2)
    c: Horizontal(g1)
    c: Horizontal(g3)
    c: Coincident(g0,g-6)
    c: PointOnObject(g1,g-4)
FEATURE [PartDesign::Pad] Pad164
  BaseFeature = -> Pocket203
  Direction = (-3e-15,0,1)
  Length = 2
  Length2 = 10
  Profile = -> Sketch232
  ReferenceAxis = -> Sketch232 [N_Axis]
  Refine = true
  Reversed = true
  Suppressed = false
  Type = 0
FEATURE [Sketcher::SketchObject] Sketch233
  ArcFitTolerance = 1e-06
  AttachmentSupport = -> [Pad164]
  ExternalGeometry = -> [Pad164]
  FullyConstrained = true
  MakeInternals = false
  MapMode = 5
  Placement = pos=(0.2,0,1.4e-15) rot=(0.57735,0.57735,0.57735;2.0944rad)
  sketch-geometry (4):
    g0: LineSegment StartX=-77.15 StartY=15.3 StartZ=0 EndX=-54.15 EndY=15.3 EndZ=0
    g1: LineSegment StartX=-54.15 StartY=15.3 StartZ=0 EndX=-54.15 EndY=13.3 EndZ=0
    g2: LineSegment StartX=-54.15 StartY=13.3 StartZ=0 EndX=-77.5786 EndY=13.3 EndZ=0
    g3: LineSegment StartX=-77.5786 StartY=13.3 StartZ=0 EndX=-77.15 EndY=15.3 EndZ=0
  constraints (10):
    c: Coincident(g0,g-6)
    c: Coincident(g0,g-4)
    c: Coincident(g1,g0)
    c: PointOnObject(g1,g-3)
    c: Coincident(g2,g1)
    c: Horizontal(g2)
    c: Coincident(g3,g2)
    c: Coincident(g3,g0)
    c: DistanceY(g1,g1) = 2
    c: PointOnObject(g2,g-6)
FEATURE [PartDesign::Pad] Pad165
  BaseFeature = -> Pad164
  Direction = (1,0,7.1e-15)
  Length = 10.8
  Length2 = 10
  Profile = -> Sketch233
  ReferenceAxis = -> Sketch233 [N_Axis]
  Refine = true
  Suppressed = false
  Type = 0
FEATURE [Sketcher::SketchObject] Sketch234
  ArcFitTolerance = 1e-06
  AttachmentSupport = -> [Pad165]
  ExternalGeometry = -> [Pad165]
  FullyConstrained = true
  MakeInternals = false
  MapMode = 5
  Placement = pos=(0.2,0,1.4e-15) rot=(0.57735,0.57735,0.57735;2.0944rad)
  sketch-geometry (4):
    g0: LineSegment StartX=-56.15 StartY=13.3 StartZ=0 EndX=-56.15 EndY=3.3 EndZ=0
    g1: LineSegment StartX=-56.15 StartY=3.3 StartZ=0 EndX=-54.15 EndY=3.3 EndZ=0
    g2: LineSegment StartX=-54.15 StartY=3.3 StartZ=0 EndX=-54.15 EndY=13.3 EndZ=0
    g3: LineSegment StartX=-54.15 StartY=13.3 StartZ=0 EndX=-56.15 EndY=13.3 EndZ=0
  constraints (11):
    c: Coincident(g0,g1)
    c: Coincident(g1,g2)
    c: Coincident(g2,g3)
    c: Coincident(g3,g0)
    c: Vertical(g0)
    c: Vertical(g2)
    c: Horizontal(g1)
    c: Horizontal(g3)
    c: Coincident(g0,g-5)
    c: PointOnObject(g1,g-4)
    c: DistanceY(g2,g2) = 10
FEATURE [PartDesign::Pad] Pad166
  BaseFeature = -> Pad165
  Direction = (1,0,7.1e-15)
  Length = 10.8
  Length2 = 10
  Profile = -> Sketch234
  ReferenceAxis = -> Sketch234 [N_Axis]
  Refine = true
  Suppressed = false
  Type = 0
FEATURE [Sketcher::SketchObject] Sketch235
  ArcFitTolerance = 1e-06
  AttachmentSupport = -> [Pad166]
  ExternalGeometry = -> [Pad166]
  FullyConstrained = true
  MakeInternals = false
  MapMode = 5
  Placement = pos=(-8.8e-14,0,15.3) rot=(0,0,1;0rad)
  sketch-geometry (4):
    g0: LineSegment StartX=8.8 StartY=-56.05 StartZ=0 EndX=0.8 EndY=-56.05 EndZ=0
    g1: LineSegment StartX=0.8 StartY=-56.05 StartZ=0 EndX=0.8 EndY=-74.05 EndZ=0
    g2: LineSegment StartX=0.8 StartY=-74.05 StartZ=0 EndX=8.8 EndY=-74.05 EndZ=0
    g3: LineSegment StartX=8.8 StartY=-74.05 StartZ=0 EndX=8.8 EndY=-56.05 EndZ=0
  constraints (12):
    c: Coincident(g0,g1)
    c: Coincident(g1,g2)
    c: Coincident(g2,g3)
    c: Coincident(g3,g0)
    c: Horizontal(g0)
    c: Horizontal(g2)
    c: Vertical(g1)
    c: Vertical(g3)
    c: DistanceX(g0,g0) = 8
    c: DistanceX(g-3,g0) = 2.9
    c: DistanceY(g0,g-3) = 1.9
    c: DistanceY(g1,g1) = 18
FEATURE [PartDesign::Pad] Pad167
  BaseFeature = -> Pad166
  Direction = (-5.8e-15,0,1)
  Length = 0.5
  Length2 = 10
  Profile = -> Sketch235
  ReferenceAxis = -> Sketch235 [N_Axis]
  Refine = true
  Suppressed = false
  Type = 0
FEATURE [Sketcher::SketchObject] Sketch236
  ArcFitTolerance = 1e-06
  AttachmentSupport = -> [Pad167]
  ExternalGeometry = -> [Pad167]
  FullyConstrained = true
  MakeInternals = false
  MapMode = 5
  Placement = pos=(-9.12e-14,0,15.8) rot=(0,0,1;0rad)
  sketch-geometry (12):
    g0: LineSegment StartX=2.7 StartY=-56.05 StartZ=0 EndX=2.7 EndY=-74.05 EndZ=0
    g1: LineSegment StartX=2.7 StartY=-74.05 StartZ=0 EndX=2.9 EndY=-74.05 EndZ=0
    g2: LineSegment StartX=2.9 StartY=-74.05 StartZ=0 EndX=2.9 EndY=-56.05 EndZ=0
    g3: LineSegment StartX=2.9 StartY=-56.05 StartZ=0 EndX=2.7 EndY=-56.05 EndZ=0
    g4: LineSegment StartX=4.7 StartY=-56.05 StartZ=0 EndX=4.7 EndY=-74.05 EndZ=0
    g5: LineSegment StartX=4.7 StartY=-74.05 StartZ=0 EndX=4.9 EndY=-74.05 EndZ=0
    g6: LineSegment StartX=4.9 StartY=-74.05 StartZ=0 EndX=4.9 EndY=-56.05 EndZ=0
    g7: LineSegment StartX=4.9 StartY=-56.05 StartZ=0 EndX=4.7 EndY=-56.05 EndZ=0
    g8: LineSegment StartX=6.7 StartY=-56.05 StartZ=0 EndX=6.7 EndY=-74.05 EndZ=0
    g9: LineSegment StartX=6.7 StartY=-74.05 StartZ=0 EndX=6.9 EndY=-74.05 EndZ=0
    g10: LineSegment StartX=6.9 StartY=-74.05 StartZ=0 EndX=6.9 EndY=-56.05 EndZ=0
    g11: LineSegment StartX=6.9 StartY=-56.05 StartZ=0 EndX=6.7 EndY=-56.05 EndZ=0
  constraints (36):
    c: Coincident(g0,g1)
    c: Coincident(g1,g2)
    c: Coincident(g2,g3)
    c: Coincident(g3,g0)
    c: Vertical(g0)
    c: Vertical(g2)
    c: Horizontal(g1)
    c: Horizontal(g3)
    c: PointOnObject(g0,g-3)
    c: PointOnObject(g1,g-5)
    c: Coincident(g4,g5)
    c: Coincident(g5,g6)
    c: Coincident(g6,g7)
    c: Coincident(g7,g4)
    c: Vertical(g4)
    c: Vertical(g6)
    c: Horizontal(g5)
    c: Horizontal(g7)
    c: PointOnObject(g4,g-3)
    c: PointOnObject(g5,g-5)
    c: Coincident(g8,g9)
    c: Coincident(g9,g10)
    c: Coincident(g10,g11)
    c: Coincident(g11,g8)
    c: Vertical(g8)
    c: Vertical(g10)
    c: Horizontal(g9)
    c: Horizontal(g11)
    c: PointOnObject(g8,g-3)
    c: PointOnObject(g9,g-5)
    c: DistanceX(g3,g3) = 0.2
    c: DistanceX(g7,g7) = 0.2
    c: DistanceX(g11,g11) = 0.2
    c: DistanceX(g-6,g0) = 1.9
    c: DistanceX(g10,g-4) = 1.9
    c: DistanceX(g2,g4) = 1.8
FEATURE [PartDesign::Pocket] Pocket204
  BaseFeature = -> Pad167
  Direction = (5.8e-15,0,-1)
  Length = 0.2
  Length2 = 5
  Profile = -> Sketch236
  ReferenceAxis = -> Sketch236 [N_Axis]
  Refine = true
  Suppressed = false
  Type = 0
FEATURE [Sketcher::SketchObject] Sketch237
  ArcFitTolerance = 1e-06
  AttachmentSupport = -> [Pocket204]
  ExternalGeometry = -> [Pocket204]
  FullyConstrained = true
  MakeInternals = false
  MapMode = 5
  Placement = pos=(-8.8e-14,0,15.3) rot=(0,0,1;0rad)
  sketch-geometry (4):
    g0: LineSegment StartX=11 StartY=-54.15 StartZ=0 EndX=8.8 EndY=-54.15 EndZ=0
    g1: LineSegment StartX=8.8 StartY=-54.15 StartZ=0 EndX=8.8 EndY=-77.5786 EndZ=0
    g2: LineSegment StartX=8.8 StartY=-77.5786 StartZ=0 EndX=11 EndY=-77.5786 EndZ=0
    g3: LineSegment StartX=11 StartY=-77.5786 StartZ=0 EndX=11 EndY=-54.15 EndZ=0
  constraints (11):
    c: Coincident(g0,g1)
    c: Coincident(g1,g2)
    c: Coincident(g2,g3)
    c: Coincident(g3,g0)
    c: Horizontal(g0)
    c: Horizontal(g2)
    c: Vertical(g1)
    c: Vertical(g3)
    c: Coincident(g0,g-4)
    c: PointOnObject(g1,g-5)
    c: PointOnObject(g-6,g1)
FEATURE [PartDesign::Pocket] Pocket205
  BaseFeature = -> Pocket204
  Direction = (5.8e-15,0,-1)
  Length = 1
  Length2 = 5
  Profile = -> Sketch237
  ReferenceAxis = -> Sketch237 [N_Axis]
  Refine = true
  Suppressed = false
  Type = 0
FEATURE [Sketcher::SketchObject] Sketch238
  ArcFitTolerance = 1e-06
  AttachmentSupport = -> [Pocket205]
  ExternalGeometry = -> [Pocket205]
  FullyConstrained = true
  MakeInternals = false
  MapMode = 5
  Placement = pos=(-6.89e-14,0,13.3) rot=(1,0,0;3.14159rad)
  sketch-geometry (4):
    g0: LineSegment StartX=6.79538 StartY=71.9786 StartZ=0 EndX=2.79538 EndY=71.9786 EndZ=0
    g1: LineSegment StartX=2.79538 StartY=71.9786 StartZ=0 EndX=2.79538 EndY=58.4786 EndZ=0
    g2: LineSegment StartX=2.79538 StartY=58.4786 StartZ=0 EndX=6.79538 EndY=58.4786 EndZ=0
    g3: LineSegment StartX=6.79538 StartY=58.4786 StartZ=0 EndX=6.79538 EndY=71.9786 EndZ=0
  constraints (12):
    c: Coincident(g0,g1)
    c: Coincident(g1,g2)
    c: Coincident(g2,g3)
    c: Coincident(g3,g0)
    c: Horizontal(g0)
    c: Horizontal(g2)
    c: Vertical(g1)
    c: Vertical(g3)
    c: DistanceX(g0,g0) = 4
    c: DistanceY(g3,g3) = 13.5
    c: DistanceY(g0,g-4) = 5.6
    c: DistanceX(g-6,g0) = 5.03
FEATURE [PartDesign::Pocket] Pocket072
  BaseFeature = -> Pocket205
  Direction = (-5.2e-15,0,1)
  Length = 1
  Length2 = 5
  Profile = -> Sketch238
  ReferenceAxis = -> Sketch238 [N_Axis]
  Refine = true
  Suppressed = false
  Type = 0
FEATURE [Sketcher::SketchObject] Sketch239
  ArcFitTolerance = 1e-06
  AttachmentSupport = -> [Pocket072]
  ExternalGeometry = -> [Pocket072]
  FullyConstrained = true
  MakeInternals = false
  MapMode = 5
  Placement = pos=(5.14e-14,-54.15,-3.14e-14) rot=(0,0.707107,0.707107;3.14159rad)
  sketch-geometry (4):
    g0: LineSegment StartX=3.55 StartY=-8.55 StartZ=0 EndX=-0.2 EndY=-8.55 EndZ=0
    g1: LineSegment StartX=-0.2 StartY=-8.55 StartZ=0 EndX=-0.2 EndY=-9.55 EndZ=0
    g2: LineSegment StartX=-0.2 StartY=-9.55 StartZ=0 EndX=3.55 EndY=-9.55 EndZ=0
    g3: LineSegment StartX=3.55 StartY=-9.55 StartZ=0 EndX=3.55 EndY=-8.55 EndZ=0
  constraints (10):
    c: Coincident(g0,g1)
    c: Coincident(g1,g2)
    c: Coincident(g2,g3)
    c: Coincident(g3,g0)
    c: Horizontal(g0)
    c: Horizontal(g2)
    c: Vertical(g1)
    c: Coincident(g0,g-3)
    c: PointOnObject(g1,g-4)
    c: Coincident(g2,g-3)
FEATURE [PartDesign::Pad] Pad168
  BaseFeature = -> Pocket072
  Direction = (0,1,-2e-16)
  Length = 0.25
  Length2 = 10
  Profile = -> Sketch239
  ReferenceAxis = -> Sketch239 [N_Axis]
  Refine = true
  Suppressed = false
  Type = 0
FEATURE [PartDesign::Fillet] Fillet016
  Base = -> Pad168 [Edge85,Edge186]
  BaseFeature = -> Pad168
  Radius = 0.24
  Refine = true
  SupportTransform = false
  Suppressed = false
  UseAllEdges = false
FEATURE [Sketcher::SketchObject] Sketch240
  ArcFitTolerance = 1e-06
  AttachmentSupport = -> [Fillet016]
  ExternalGeometry = -> [Fillet016]
  FullyConstrained = true
  MakeInternals = false
  MapMode = 5
  Placement = pos=(-6.89e-14,0,13.3) rot=(1,0,0;3.14159rad)
  sketch-geometry (4):
    g0: LineSegment StartX=6.79538 StartY=66.1286 StartZ=0 EndX=6.79538 EndY=64.3286 EndZ=0
    g1: LineSegment StartX=6.79538 StartY=64.3286 StartZ=0 EndX=9.29538 EndY=64.3286 EndZ=0
    g2: LineSegment StartX=9.29538 StartY=64.3286 StartZ=0 EndX=9.29538 EndY=66.1286 EndZ=0
    g3: LineSegment StartX=9.29538 StartY=66.1286 StartZ=0 EndX=6.79538 EndY=66.1286 EndZ=0
  constraints (13):
    c: DistanceY(g-3,g-3) = 13.5
    c: Coincident(g0,g1)
    c: Coincident(g1,g2)
    c: Coincident(g2,g3)
    c: Coincident(g3,g0)
    c: Vertical(g0)
    c: Vertical(g2)
    c: Horizontal(g1)
    c: Horizontal(g3)
    c: PointOnObject(g0,g-3)
    c: DistanceY(g2,g2) = 1.8
    c: DistanceX(g3,g3) = 2.5
    c: DistanceY(g-3,g0) = 5.85
FEATURE [PartDesign::Pad] Pad169
  BaseFeature = -> Fillet016
  Direction = (5.2e-15,0,-1)
  Length = 1.7
  Length2 = 10
  Profile = -> Sketch240
  ReferenceAxis = -> Sketch240 [N_Axis]
  Refine = true
  Suppressed = false
  Type = 0
FEATURE [Sketcher::SketchObject] Sketch241
  ArcFitTolerance = 1e-06
  AttachmentSupport = -> [Pad169]
  ExternalGeometry = -> [Pad169]
  FullyConstrained = true
  MakeInternals = false
  MapMode = 5
  Placement = pos=(-6.89e-14,0,13.3) rot=(1,0,0;3.14159rad)
  sketch-geometry (4):
    g0: LineSegment StartX=6.79538 StartY=66.1286 StartZ=0 EndX=11 EndY=66.1286 EndZ=0
    g1: LineSegment StartX=11 StartY=66.1286 StartZ=0 EndX=11 EndY=68.4286 EndZ=0
    g2: LineSegment StartX=11 StartY=68.4286 StartZ=0 EndX=6.79538 EndY=68.4286 EndZ=0
    g3: LineSegment StartX=6.79538 StartY=68.4286 StartZ=0 EndX=6.79538 EndY=66.1286 EndZ=0
  constraints (11):
    c: Coincident(g0,g1)
    c: Coincident(g1,g2)
    c: Coincident(g2,g3)
    c: Coincident(g3,g0)
    c: Horizontal(g0)
    c: Horizontal(g2)
    c: Vertical(g1)
    c: Vertical(g3)
    c: Coincident(g0,g-6)
    c: PointOnObject(g1,g-3)
    c: DistanceY(g1,g1) = 2.3
FEATURE [PartDesign::Pad] Pad170
  BaseFeature = -> Pad169
  Direction = (5.2e-15,0,-1)
  Length = 0.7
  Length2 = 10
  Profile = -> Sketch241
  ReferenceAxis = -> Sketch241 [N_Axis]
  Refine = true
  Suppressed = false
  Type = 0
FEATURE [PartDesign::Body] Body022  label="Cab"
  AllowCompound = false
  Group = -> [Binder014,Sketch222,Pad160,Sketch223,Pad161,Sketch224,Pocket064,Fillet015,Sketch225,Pocket199,Sketch226,Pocket200,Sketch227,Pad162,Sketch228,Pad163,Sketch229,Pocket201,Sketch230,Pocket202,Sketch231,Pocket203,Sketch232,Pad164,Sketch233,Pad165,Sketch234,Pad166,Sketch235,Pad167,Sketch236,Pocket204,Sketch237,Pocket205,Sketch238,Pocket072,Sketch239,Pad168,Fillet016,Sketch240,Pad169,Sketch241,Pad170,+19 more]
  Origin = -> Origin024
  Placement = pos=(33,38,0) rot=(0,0,1;0rad)
  Tip = -> Pocket081
COMPONENT P13 — recipe-attached ("Windshield", modeled in this document).
Construction recipe (the document's own serialized feature program — sketch geometry with constraints, then the solid features built on it; lengths are millimeters unless a unit is written):

FEATURE [PartDesign::SubShapeBinder] Binder016
  BindCopyOnChange = 0
  BindMode = 2
  ClaimChildren = false
  Context = -> Body024 [Binder016.]
  Fuse = false
  MakeFace = true
  OffsetFill = false
  OffsetIntersection = false
  OffsetJoinType = 0
  OffsetOpenResult = false
  PartialLoad = false
  Refine = true
  Relative = true
  _Version = 2
FEATURE [Sketcher::SketchObject] Sketch263
  ArcFitTolerance = 1e-06
  AttachmentSupport = -> [Binder016]
  ExternalGeometry = -> [Binder016]
  FullyConstrained = true
  MakeInternals = false
  MapMode = 5
  Placement = pos=(0.2,0,1.4e-15) rot=(0.57735,0.57735,0.57735;2.0944rad)
  sketch-geometry (4):
    g0: LineSegment StartX=-79.85 StartY=4.2 StartZ=0 EndX=-77.85 EndY=4.2 EndZ=0
    g1: LineSegment StartX=-77.85 StartY=4.2 StartZ=0 EndX=-75.9 EndY=13.3 EndZ=0
    g2: LineSegment StartX=-75.9 StartY=13.3 StartZ=0 EndX=-77.5786 EndY=13.3 EndZ=0
    g3: LineSegment StartX=-77.5786 StartY=13.3 StartZ=0 EndX=-79.85 EndY=4.2 EndZ=0
  constraints (8):
    c: Coincident(g0,g-4)
    c: Coincident(g0,g-6)
    c: Coincident(g1,g0)
    c: Coincident(g1,g-6)
    c: Coincident(g2,g1)
    c: Coincident(g2,g-5)
    c: Coincident(g3,g2)
    c: Coincident(g3,g0)
FEATURE [PartDesign::Pad] Pad203
  Direction = (1,0,7.1e-15)
  Length = 21.6
  Length2 = 10
  Profile = -> Sketch263
  ReferenceAxis = -> Sketch263 [N_Axis]
  Refine = true
  Suppressed = false
  Type = 0
FEATURE [PartDesign::Pad] Pad204
  BaseFeature = -> Pad203
  Direction = (7.1e-15,0,-1)
  Length = 1.2
  Length2 = 10
  Profile = -> Pad203 [Face1]
  Refine = true
  Suppressed = false
  Type = 0
FEATURE [Sketcher::SketchObject] Sketch264
  ArcFitTolerance = 1e-06
  AttachmentSupport = -> [Pad204]
  ExternalGeometry = -> [Pad204]
  FullyConstrained = true
  MakeInternals = false
  MapMode = 5
  Placement = pos=(0,-77.85,0) rot=(0,0.707107,0.707107;3.14159rad)
  sketch-geometry (8):
    g0: LineSegment StartX=-20.9 StartY=4.2 StartZ=0 EndX=-20.9 EndY=3 EndZ=0
    g1: LineSegment StartX=-20.9 StartY=3 StartZ=0 EndX=-18.9 EndY=3 EndZ=0
    g2: LineSegment StartX=-18.9 StartY=3 StartZ=0 EndX=-18.9 EndY=4.2 EndZ=0
    g3: LineSegment StartX=-18.9 StartY=4.2 StartZ=0 EndX=-20.9 EndY=4.2 EndZ=0
    g4: LineSegment StartX=-1.1 StartY=4.2 StartZ=0 EndX=-3.1 EndY=4.2 EndZ=0
    g5: LineSegment StartX=-3.1 StartY=4.2 StartZ=0 EndX=-3.1 EndY=3 EndZ=0
    g6: LineSegment StartX=-3.1 StartY=3 StartZ=0 EndX=-1.1 EndY=3 EndZ=0
    g7: LineSegment StartX=-1.1 StartY=3 StartZ=0 EndX=-1.1 EndY=4.2 EndZ=0
  constraints (24):
    c: Coincident(g0,g1)
    c: Coincident(g1,g2)
    c: Coincident(g2,g3)
    c: Coincident(g3,g0)
    c: Vertical(g0)
    c: Vertical(g2)
    c: Horizontal(g1)
    c: Horizontal(g3)
    c: PointOnObject(g0,g-3)
    c: PointOnObject(g1,g-5)
    c: Coincident(g4,g5)
    c: Coincident(g5,g6)
    c: Coincident(g6,g7)
    c: Coincident(g7,g4)
    c: Horizontal(g4)
    c: Horizontal(g6)
    c: Vertical(g5)
    c: Vertical(g7)
    c: PointOnObject(g4,g-3)
    c: PointOnObject(g5,g-5)
    c: DistanceX(g4,g4) = 2
    c: DistanceX(g3,g3) = 2
    c: DistanceX(g-4,g0) = 0.9
    c: DistanceX(g4,g-6) = 0.9
FEATURE [PartDesign::Pad] Pad205
  BaseFeature = -> Pad204
  Direction = (0,1,-2e-16)
  Length = 2
  Length2 = 10
  Profile = -> Sketch264
  ReferenceAxis = -> Sketch264 [N_Axis]
  Refine = true
  Suppressed = false
  Type = 0
FEATURE [Sketcher::SketchObject] Sketch265
  ArcFitTolerance = 1e-06
  AttachmentSupport = -> [Pad205]
  ExternalGeometry = -> [Pad205]
  FullyConstrained = true
  MakeInternals = false
  MapMode = 5
  Placement = pos=(20.9,0,0) rot=(0.57735,0.57735,0.57735;2.0944rad)
  sketch-geometry (3):
    g0: LineSegment StartX=-77.85 StartY=4.2 StartZ=0 EndX=-75.85 EndY=4.2 EndZ=0
    g1: LineSegment StartX=-75.85 StartY=4.2 StartZ=0 EndX=-75.85 EndY=3 EndZ=0
    g2: LineSegment StartX=-75.85 StartY=3 StartZ=0 EndX=-77.85 EndY=4.2 EndZ=0
  constraints (6):
    c: Coincident(g0,g-3)
    c: Coincident(g0,g-4)
    c: Coincident(g1,g0)
    c: Coincident(g1,g-4)
    c: Coincident(g2,g1)
    c: Coincident(g2,g0)
FEATURE [PartDesign::Pocket] Pocket088
  BaseFeature = -> Pad205
  Direction = (-1,0,0)
  Length = 20
  Length2 = 5
  Profile = -> Sketch265
  ReferenceAxis = -> Sketch265 [N_Axis]
  Refine = true
  Suppressed = false
  Type = 0
FEATURE [Sketcher::SketchObject] Sketch266
  ArcFitTolerance = 1e-06
  AttachmentSupport = -> [Pocket088]
  ExternalGeometry = -> [Pocket088]
  FullyConstrained = true
  MakeInternals = false
  MapMode = 5
  Placement = pos=(-2.09e-14,-2.24e-14,3) rot=(1,0,0;3.14159rad)
  sketch-geometry (8):
    g0: LineSegment StartX=0.2 StartY=79.85 StartZ=0 EndX=0.2 EndY=77.85 EndZ=0
    g1: LineSegment StartX=0.2 StartY=77.85 StartZ=0 EndX=4.2 EndY=77.85 EndZ=0
    g2: LineSegment StartX=4.2 StartY=77.85 StartZ=0 EndX=4.2 EndY=79.85 EndZ=0
    g3: LineSegment StartX=4.2 StartY=79.85 StartZ=0 EndX=0.2 EndY=79.85 EndZ=0
    g4: LineSegment StartX=21.8 StartY=79.85 StartZ=0 EndX=17.8 EndY=79.85 EndZ=0
    g5: LineSegment StartX=17.8 StartY=79.85 StartZ=0 EndX=17.8 EndY=77.85 EndZ=0
    g6: LineSegment StartX=17.8 StartY=77.85 StartZ=0 EndX=21.8 EndY=77.85 EndZ=0
    g7: LineSegment StartX=21.8 StartY=77.85 StartZ=0 EndX=21.8 EndY=79.85 EndZ=0
  constraints (22):
    c: Coincident(g0,g1)
    c: Coincident(g1,g2)
    c: Coincident(g2,g3)
    c: Coincident(g3,g0)
    c: Vertical(g0)
    c: Vertical(g2)
    c: Horizontal(g1)
    c: Horizontal(g3)
    c: Coincident(g0,g-7)
    c: PointOnObject(g1,g-5)
    c: Coincident(g4,g5)
    c: Coincident(g5,g6)
    c: Coincident(g6,g7)
    c: Coincident(g7,g4)
    c: Horizontal(g4)
    c: Horizontal(g6)
    c: Vertical(g5)
    c: Vertical(g7)
    c: Coincident(g4,g-6)
    c: PointOnObject(g5,g-5)
    c: DistanceX(g6,g6) = 4
    c: DistanceX(g1,g1) = 4
FEATURE [PartDesign::Pad] Pad206
  BaseFeature = -> Pocket088
  Direction = (7e-15,7.5e-15,-1)
  Length = 3.5
  Length2 = 10
  Profile = -> Sketch266
  ReferenceAxis = -> Sketch266 [N_Axis]
  Refine = true
  Suppressed = false
  Type = 0
FEATURE [Sketcher::SketchObject] Sketch267
  ArcFitTolerance = 1e-06
  AttachmentSupport = -> [Pad206]
  ExternalGeometry = -> [Pad206]
  FullyConstrained = true
  MakeInternals = false
  MapMode = 5
  Placement = pos=(21.8,5e-15,1.574e-13) rot=(0.57735,0.57735,0.57735;2.0944rad)
  sketch-geometry (4):
    g0: LineSegment StartX=-77.85 StartY=3 StartZ=0 EndX=-77.95 EndY=3 EndZ=0
    g1: LineSegment StartX=-77.95 StartY=3 StartZ=0 EndX=-77.95 EndY=-0.5 EndZ=0
    g2: LineSegment StartX=-77.95 StartY=-0.5 StartZ=0 EndX=-77.85 EndY=-0.5 EndZ=0
    g3: LineSegment StartX=-77.85 StartY=-0.5 StartZ=0 EndX=-77.85 EndY=3 EndZ=0
  constraints (12):
    c: Coincident(g0,g1)
    c: Coincident(g1,g2)
    c: Coincident(g2,g3)
    c: Coincident(g3,g0)
    c: Horizontal(g0)
    c: Horizontal(g2)
    c: Vertical(g1)
    c: Vertical(g3)
    c: PointOnObject(g0,g-3)
    c: PointOnObject(g1,g-4)
    c: DistanceY(g1,g1) = 3.5
    c: DistanceX(g0,g0) = 0.1
FEATURE [PartDesign::Pocket] Pocket089
  BaseFeature = -> Pad206
  Direction = (-1,-1e-16,-7.2e-15)
  Length = 22
  Length2 = 5
  Profile = -> Sketch267
  ReferenceAxis = -> Sketch267 [N_Axis]
  Refine = true
  Suppressed = false
  Type = 0
FEATURE [Sketcher::SketchObject] Sketch268
  ArcFitTolerance = 1e-06
  AttachmentSupport = -> [Pocket089]
  ExternalGeometry = -> [Pocket089]
  FullyConstrained = true
  MakeInternals = false
  MapMode = 5
  Placement = pos=(8.6e-15,-77.95,-8.6e-15) rot=(0,0.707107,0.707107;3.14159rad)
  sketch-geometry (2):
    g0: Circle CenterX=-19.55 CenterY=1.2 CenterZ=0 NormalX=0 NormalY=0 NormalZ=1 AngleXU=0 Radius=0.7
    g1: Circle CenterX=-2.45 CenterY=1.2 CenterZ=0 NormalX=0 NormalY=0 NormalZ=1 AngleXU=0 Radius=0.7
  constraints (6):
    c: Diameter(g1) = 1.4
    c: Diameter(g0) = 1.4
    c: DistanceX(g-4,g0) = 2.25
    c: DistanceY(g0,g-4) = 1.8
    c: DistanceY(g1,g-7) = 1.8
    c: DistanceX(g1,g-7) = 2.25
FEATURE [PartDesign::Pocket] Pocket090
  BaseFeature = -> Pocket089
  Direction = (0,-1,2e-16)
  Length = 5
  Length2 = 5
  Profile = -> Sketch268
  ReferenceAxis = -> Sketch268 [N_Axis]
  Refine = true
  Suppressed = false
  Type = 0
FEATURE [PartDesign::Fillet] Fillet020
  Base = -> Pocket090 [Edge34,Edge60,Edge54,Edge29]
  BaseFeature = -> Pocket090
  Radius = 1
  Refine = true
  SupportTransform = false
  Suppressed = false
  UseAllEdges = false
FEATURE [PartDesign::Body] Body024  label="Windshield"
  AllowCompound = false
  Group = -> [Binder016,Sketch263,Pad203,Pad204,Sketch264,Pad205,Sketch265,Pocket088,Sketch266,Pad206,Sketch267,Pocket089,Sketch268,Pocket090,Fillet020]
  Origin = -> Origin026
  Placement = pos=(33,38,-1.42e-14) rot=(0,0,1;0rad)
  Tip = -> Fillet020
COMPONENT P14 — recipe-attached ("Pre_Left_Shoulder", modeled in this document).
Construction recipe (the document's own serialized feature program — sketch geometry with constraints, then the solid features built on it; lengths are millimeters unless a unit is written):

FEATURE [Sketcher::SketchObject] Sketch269
  ArcFitTolerance = 1e-06
  AttachmentSupport = -> [XY_Plane028]
  FullyConstrained = true
  MakeInternals = false
  MapMode = 5
  sketch-geometry (8):
    g0: LineSegment StartX=-3.15 StartY=3.2 StartZ=0 EndX=-3.15 EndY=-3.2 EndZ=0
    g1: LineSegment StartX=-3.15 StartY=-3.2 StartZ=0 EndX=3.15 EndY=-3.2 EndZ=0
    g2: LineSegment StartX=3.15 StartY=-3.2 StartZ=0 EndX=3.15 EndY=1.2 EndZ=0
    g3: LineSegment StartX=3.15 StartY=1.2 StartZ=0 EndX=-0.35 EndY=1.2 EndZ=0
    g4: LineSegment StartX=-0.35 StartY=1.2 StartZ=0 EndX=-0.35 EndY=2.2 EndZ=0
    g5: LineSegment StartX=-0.35 StartY=2.2 StartZ=0 EndX=3.15 EndY=2.2 EndZ=0
    g6: LineSegment StartX=3.15 StartY=2.2 StartZ=0 EndX=3.15 EndY=3.2 EndZ=0
    g7: LineSegment StartX=3.15 StartY=3.2 StartZ=0 EndX=-3.15 EndY=3.2 EndZ=0
  constraints (24):
    c: Vertical(g0)
    c: Coincident(g1,g0)
    c: Horizontal(g1)
    c: Coincident(g2,g1)
    c: Vertical(g2)
    c: Coincident(g3,g2)
    c: Horizontal(g3)
    c: Coincident(g4,g3)
    c: Vertical(g4)
    c: Coincident(g5,g4)
    c: Horizontal(g5)
    c: Coincident(g6,g5)
    c: Vertical(g6)
    c: Horizontal(g7)
    c: Coincident(g0,g7)
    c: Coincident(g7,g6)
    c: DistanceY(g0,g0) = 6.4
    c: DistanceX(g1,g1) = 6.3
    c: DistanceY(g6,g6) = 1
    c: DistanceY(g4,g4) = 1
    c: DistanceX(g7,g7) = 6.3
    c: DistanceX(g3,g3) = 3.5
    c: DistanceX(g0,g-1) = 3.15
    c: DistanceY(g0,g-1) = 3.2
FEATURE [PartDesign::Pad] Pad198
  Direction = (0,0,1)
  Length = 8
  Length2 = 10
  Profile = -> Sketch269
  ReferenceAxis = -> Sketch269 [N_Axis]
  Refine = true
  Suppressed = false
  Type = 0
FEATURE [Sketcher::SketchObject] Sketch270
  ArcFitTolerance = 1e-06
  AttachmentSupport = -> [Pad198]
  ExternalGeometry = -> [Pad198]
  FullyConstrained = true
  MakeInternals = false
  MapMode = 5
  Placement = pos=(0,3.2,0) rot=(0,0.707107,0.707107;3.14159rad)
  sketch-geometry (8):
    g0: LineSegment StartX=-2.5 StartY=6.5 StartZ=0 EndX=-2.5 EndY=1.5 EndZ=0
    g1: LineSegment StartX=-2.5 StartY=1.5 StartZ=0 EndX=-1 EndY=1.5 EndZ=0
    g2: LineSegment StartX=-1 StartY=1.5 StartZ=0 EndX=-1 EndY=6.5 EndZ=0
    g3: LineSegment StartX=-1 StartY=6.5 StartZ=0 EndX=-2.5 EndY=6.5 EndZ=0
    g4: LineSegment StartX=1 StartY=6.5 StartZ=0 EndX=1 EndY=1.5 EndZ=0
    g5: LineSegment StartX=1 StartY=1.5 StartZ=0 EndX=2.5 EndY=1.5 EndZ=0
    g6: LineSegment StartX=2.5 StartY=1.5 StartZ=0 EndX=2.5 EndY=6.5 EndZ=0
    g7: LineSegment StartX=2.5 StartY=6.5 StartZ=0 EndX=1 EndY=6.5 EndZ=0
  constraints (26):
    c: Coincident(g0,g1)
    c: Coincident(g1,g2)
    c: Coincident(g2,g3)
    c: Coincident(g3,g0)
    c: Vertical(g0)
    c: Vertical(g2)
    c: Horizontal(g1)
    c: Horizontal(g3)
    c: Coincident(g4,g5)
    c: Coincident(g5,g6)
    c: Coincident(g6,g7)
    c: Coincident(g7,g4)
    c: Vertical(g4)
    c: Vertical(g6)
    c: Horizontal(g5)
    c: Horizontal(g7)
    c: DistanceX(g1,g1) = 1.5
    c: DistanceX(g5,g5) = 1.5
    c: DistanceY(g0,g0) = 5
    c: DistanceY(g4,g4) = 5
    c: DistanceX(g-3,g-3) = 6.3
    c: DistanceX(g1,g-1) = 1
    c: DistanceX(g-1,g4) = 1
    c: DistanceY(g-4,g-4) = 8
    c: DistanceY(g-4,g5) = 1.5
    c: DistanceY(g-3,g0) = 1.5
FEATURE [PartDesign::Pad] Pad199
  BaseFeature = -> Pad198
  Direction = (0,1,-2e-16)
  Length = 0.6
  Length2 = 10
  Profile = -> Sketch270
  ReferenceAxis = -> Sketch270 [N_Axis]
  Refine = true
  Suppressed = false
  Type = 0
FEATURE [Sketcher::SketchObject] Sketch271
  ArcFitTolerance = 1e-06
  AttachmentSupport = -> [Pad199]
  ExternalGeometry = -> [Pad199]
  FullyConstrained = true
  MakeInternals = false
  MapMode = 5
  Placement = pos=(0,-3.2,0) rot=(1,0,0;1.5708rad)
  sketch-geometry (4):
    g0: LineSegment StartX=3.15 StartY=6 StartZ=0 EndX=0.15 EndY=6 EndZ=0
    g1: LineSegment StartX=0.15 StartY=6 StartZ=0 EndX=0.15 EndY=2 EndZ=0
    g2: LineSegment StartX=0.15 StartY=2 StartZ=0 EndX=3.15 EndY=2 EndZ=0
    g3: LineSegment StartX=3.15 StartY=2 StartZ=0 EndX=3.15 EndY=6 EndZ=0
  constraints (12):
    c: Coincident(g0,g1)
    c: Coincident(g1,g2)
    c: Coincident(g2,g3)
    c: Coincident(g3,g0)
    c: Horizontal(g0)
    c: Horizontal(g2)
    c: Vertical(g1)
    c: Vertical(g3)
    c: PointOnObject(g0,g-3)
    c: DistanceY(g-3,g2) = 2
    c: DistanceY(g0,g-3) = 2
    c: DistanceX(g0,g0) = 3
FEATURE [PartDesign::Pad] Pad200
  BaseFeature = -> Pad199
  Direction = (0,-1,2e-16)
  Length = 2
  Length2 = 10
  Profile = -> Sketch271
  ReferenceAxis = -> Sketch271 [N_Axis]
  Refine = true
  Suppressed = false
  Type = 0
FEATURE [Sketcher::SketchObject] Sketch302
  ArcFitTolerance = 1e-06
  AttachmentSupport = -> [Pad200]
  ExternalGeometry = -> [Pad200]
  FullyConstrained = true
  MakeInternals = false
  MapMode = 5
  Placement = pos=(-3.15,0,0) rot=(0.57735,-0.57735,-0.57735;2.0944rad)
  sketch-geometry (1):
    g0: Circle CenterX=0 CenterY=4 CenterZ=0 NormalX=0 NormalY=0 NormalZ=1 AngleXU=0 Radius=0.9
  constraints (4):
    c: PointOnObject(g0,g-2)
    c: Diameter(g0) = 1.8
    c: DistanceY(g-3,g-3) = 8
    c: DistanceY(g-1,g0) = 4
FEATURE [PartDesign::Pocket] Pocket130
  BaseFeature = -> Pad200
  Direction = (1,0,0)
  Length = 7
  Length2 = 5
  Profile = -> Sketch302
  ReferenceAxis = -> Sketch302 [N_Axis]
  Refine = true
  Suppressed = false
  Type = 0
FEATURE [PartDesign::Body] Body026  label="Pre_Left_Shoulder"
  AllowCompound = false
  Group = -> [Sketch269,Pad198,Sketch270,Pad199,Sketch271,Pad200,Sketch302,Pocket130]
  Origin = -> Origin028
  Placement = pos=(-46,35,-10) rot=(0,0,1;0rad)
  Tip = -> Pocket130
COMPONENT P15 — recipe-attached ("Grill", modeled in this document).
Construction recipe (the document's own serialized feature program — sketch geometry with constraints, then the solid features built on it; lengths are millimeters unless a unit is written):

FEATURE [PartDesign::SubShapeBinder] Binder015
  BindCopyOnChange = 0
  BindMode = 2
  ClaimChildren = false
  Context = -> Body027 [Binder015.]
  Fuse = false
  MakeFace = true
  OffsetFill = false
  OffsetIntersection = false
  OffsetJoinType = 0
  OffsetOpenResult = false
  PartialLoad = false
  Refine = true
  Relative = true
  _Version = 2
FEATURE [Sketcher::SketchObject] Sketch256
  ArcFitTolerance = 1e-06
  AttachmentSupport = -> [Binder015]
  ExternalGeometry = -> [Binder015]
  FullyConstrained = true
  MakeInternals = false
  MapMode = 5
  Placement = pos=(2.16e-14,-80.05,3.066e-13) rot=(1,0,0;1.5708rad)
  sketch-geometry (4):
    g0: LineSegment StartX=0.2 StartY=4.2 StartZ=0 EndX=0.2 EndY=-11 EndZ=0
    g1: LineSegment StartX=0.2 StartY=-11 StartZ=0 EndX=21.8 EndY=-11 EndZ=0
    g2: LineSegment StartX=21.8 StartY=-11 StartZ=0 EndX=21.8 EndY=4.2 EndZ=0
    g3: LineSegment StartX=21.8 StartY=4.2 StartZ=0 EndX=0.2 EndY=4.2 EndZ=0
  constraints (12):
    c: Coincident(g0,g1)
    c: Coincident(g1,g2)
    c: Coincident(g2,g3)
    c: Coincident(g3,g0)
    c: Vertical(g0)
    c: Vertical(g2)
    c: Horizontal(g1)
    c: Horizontal(g3)
    c: DistanceX(g0,g-4) = 10.8
    c: DistanceX(g-4,g2) = 10.8
    c: DistanceY(g-4,g0) = 8.2
    c: DistanceY(g0,g-4) = 7
FEATURE [PartDesign::Pad] Pad172
  Direction = (0,-1,4e-15)
  Length = 2
  Length2 = 10
  Profile = -> Sketch256
  ReferenceAxis = -> Sketch256 [N_Axis]
  Refine = true
  Suppressed = false
  Type = 0
FEATURE [Sketcher::SketchObject] Sketch257
  ArcFitTolerance = 1e-06
  AttachmentSupport = -> [Pad172]
  ExternalGeometry = -> [Binder015]
  FullyConstrained = true
  MakeInternals = false
  MapMode = 5
  Placement = pos=(0,-80.05,2.994e-13) rot=(0,0.707107,0.707107;3.14159rad)
  sketch-geometry (1):
    g0: Circle CenterX=-11 CenterY=-4 CenterZ=0 NormalX=0 NormalY=0 NormalZ=1 AngleXU=0 Radius=2
  constraints (2):
    c: Coincident(g0,g-3)
    c: Equal(g0,g-3)
FEATURE [PartDesign::Pad] Pad173
  BaseFeature = -> Pad172
  Direction = (0,1,-4e-15)
  Length = 4
  Length2 = 10
  Profile = -> Sketch257
  ReferenceAxis = -> Sketch257 [N_Axis]
  Refine = true
  Suppressed = false
  Type = 0
FEATURE [Sketcher::SketchObject] Sketch258
  ArcFitTolerance = 1e-06
  AttachmentSupport = -> [Pad173]
  ExternalGeometry = -> [Pad173]
  FullyConstrained = true
  MakeInternals = false
  MapMode = 5
  Placement = pos=(-1.802e-13,-76.05,3.118e-13) rot=(0,0.707107,0.707107;3.14159rad)
  sketch-geometry (1):
    g0: Circle CenterX=-11 CenterY=-4 CenterZ=0 NormalX=0 NormalY=0 NormalZ=1 AngleXU=0 Radius=0.75
  constraints (2):
    c: Coincident(g0,g-3)
    c: Radius(g0) = 0.75
FEATURE [PartDesign::Pocket] Pocket086
  BaseFeature = -> Pad173
  Direction = (-2.4e-15,-1,4e-15)
  Length = 4
  Length2 = 5
  Profile = -> Sketch258
  ReferenceAxis = -> Sketch258 [N_Axis]
  Refine = true
  Suppressed = false
  Type = 0
FEATURE [Sketcher::SketchObject] Sketch259
  ArcFitTolerance = 1e-06
  AttachmentSupport = -> [Pocket086]
  ExternalGeometry = -> [Pocket086]
  FullyConstrained = true
  MakeInternals = false
  MapMode = 5
  Placement = pos=(0,-80.05,2.994e-13) rot=(0,0.707107,0.707107;3.14159rad)
  sketch-geometry (2):
    g0: Circle CenterX=-19.55 CenterY=1.2 CenterZ=0 NormalX=0 NormalY=0 NormalZ=1 AngleXU=0 Radius=0.65
    g1: Circle CenterX=-2.45 CenterY=1.2 CenterZ=0 NormalX=0 NormalY=0 NormalZ=1 AngleXU=0 Radius=0.65
  constraints (6):
    c: Diameter(g0) = 1.3
    c: Diameter(g1) = 1.3
    c: DistanceX(g1,g-3) = 2.25
    c: DistanceX(g-3,g0) = 2.25
    c: DistanceY(g0,g-3) = 3
    c: DistanceY(g1,g-3) = 3
FEATURE [PartDesign::Pad] Pad174
  BaseFeature = -> Pocket086
  Direction = (0,1,-4e-15)
  Length = 1.5
  Length2 = 10
  Profile = -> Sketch259
  ReferenceAxis = -> Sketch259 [N_Axis]
  Refine = true
  Suppressed = false
  Type = 0
FEATURE [Sketcher::SketchObject] Sketch260
  ArcFitTolerance = 1e-06
  AttachmentSupport = -> [Pad174]
  ExternalGeometry = -> [Pad174]
  FullyConstrained = true
  MakeInternals = false
  MapMode = 5
  Placement = pos=(0,-82.05,3.069e-13) rot=(1,0,0;1.5708rad)
  sketch-geometry (4):
    g0: LineSegment StartX=7.5 StartY=-11 StartZ=0 EndX=7.5 EndY=-12.5 EndZ=0
    g1: LineSegment StartX=7.5 StartY=-12.5 StartZ=0 EndX=14.5 EndY=-12.5 EndZ=0
    g2: LineSegment StartX=14.5 StartY=-12.5 StartZ=0 EndX=14.5 EndY=-11 EndZ=0
    g3: LineSegment StartX=14.5 StartY=-11 StartZ=0 EndX=7.5 EndY=-11 EndZ=0
  constraints (13):
    c: Coincident(g0,g1)
    c: Coincident(g1,g2)
    c: Coincident(g2,g3)
    c: Coincident(g3,g0)
    c: Vertical(g0)
    c: Vertical(g2)
    c: Horizontal(g1)
    c: Horizontal(g3)
    c: PointOnObject(g0,g-3)
    c: DistanceY(g0,g0) = 1.5
    c: DistanceX(g1,g1) = 7
    c: DistanceX(g-3,g-3) = 21.6
    c: DistanceX(g-3,g0) = 7.3
FEATURE [PartDesign::Pad] Pad175
  BaseFeature = -> Pad174
  Direction = (0,-1,4e-15)
  Length = 3
  Length2 = 10
  Profile = -> Sketch260
  ReferenceAxis = -> Sketch260 [N_Axis]
  Refine = true
  Reversed = true
  Suppressed = false
  Type = 0
FEATURE [PartDesign::Pad] Pad201
  BaseFeature = -> Pad175
  Direction = (0,-1,4e-15)
  Length = 0.7
  Length2 = 10
  Profile = -> Sketch260
  ReferenceAxis = -> Sketch260 [N_Axis]
  Refine = true
  Suppressed = false
  Type = 0
FEATURE [PartDesign::Fillet] Fillet017
  Base = -> Pad201 [Edge2,Edge43,Edge44,Edge20,Edge1,Edge5]
  BaseFeature = -> Pad201
  Radius = 1
  Refine = true
  SupportTransform = false
  Suppressed = false
  UseAllEdges = false
FEATURE [Sketcher::SketchObject] Sketch261
  ArcFitTolerance = 1e-06
  AttachmentSupport = -> [Fillet017]
  ExternalGeometry = -> [Fillet017]
  FullyConstrained = true
  MakeInternals = false
  MapMode = 5
  Placement = pos=(0,-82.05,3.397e-13) rot=(1,0,0;1.5708rad)
  sketch-geometry (68):
    g0: LineSegment StartX=0.2 StartY=-7 StartZ=0 EndX=21.8 EndY=-7 EndZ=0
    g1: LineSegment StartX=21.8 StartY=-7 StartZ=0 EndX=21.8 EndY=-6.1 EndZ=0
    g2: LineSegment StartX=21.8 StartY=-6.1 StartZ=0 EndX=18.3 EndY=-6.1 EndZ=0
    g3: LineSegment StartX=17.8 StartY=-5.6 StartZ=0 EndX=17.8 EndY=-3.6 EndZ=0
    g4: LineSegment StartX=18.3 StartY=-3.1 StartZ=0 EndX=21.8 EndY=-3.1 EndZ=0
    g5: LineSegment StartX=21.8 StartY=-3.1 StartZ=0 EndX=21.8 EndY=-2.2 EndZ=0
    g6: LineSegment StartX=21.8 StartY=-2.2 StartZ=0 EndX=0.2 EndY=-2.2 EndZ=0
    g7: LineSegment StartX=0.2 StartY=-2.2 StartZ=0 EndX=0.2 EndY=-3.1 EndZ=0
    g8: LineSegment StartX=0.2 StartY=-3.1 StartZ=0 EndX=3.7 EndY=-3.1 EndZ=0
    g9: LineSegment StartX=4.2 StartY=-3.6 StartZ=0 EndX=4.2 EndY=-5.6 EndZ=0
    g10: LineSegment StartX=3.7 StartY=-6.1 StartZ=0 EndX=0.2 EndY=-6.1 EndZ=0
    g11: LineSegment StartX=0.2 StartY=-6.1 StartZ=0 EndX=0.2 EndY=-7 EndZ=0
    g12: LineSegment StartX=16.5 StartY=-3.5 StartZ=0 EndX=5.5 EndY=-3.5 EndZ=0
    g13: LineSegment StartX=5 StartY=-4 StartZ=0 EndX=5 EndY=-5.2 EndZ=0
    g14: LineSegment StartX=5.5 StartY=-5.7 StartZ=0 EndX=16.5 EndY=-5.7 EndZ=0
    g15: LineSegment StartX=17 StartY=-5.2 StartZ=0 EndX=17 EndY=-4 EndZ=0
    g16: ArcOfCircle CenterX=5.5 CenterY=-4 CenterZ=0 NormalX=0 NormalY=0 NormalZ=1 AngleXU=0 Radius=0.5 StartAngle=1.5708 EndAngle=3.14159
    g17: GeomPoint [constr] X=5 Y=-3.5 Z=0
    g18: ArcOfCircle CenterX=5.5 CenterY=-5.2 CenterZ=0 NormalX=0 NormalY=0 NormalZ=1 AngleXU=0 Radius=0.5 StartAngle=3.14159 EndAngle=4.71239
    g19: GeomPoint [constr] X=5 Y=-5.7 Z=0
    g20: ArcOfCircle CenterX=3.7 CenterY=-5.6 CenterZ=0 NormalX=0 NormalY=0 NormalZ=1 AngleXU=0 Radius=0.5 StartAngle=4.71239 EndAngle=6.28319
    g21: GeomPoint [constr] X=4.2 Y=-6.1 Z=0
    g22: ArcOfCircle CenterX=3.7 CenterY=-3.6 CenterZ=0 NormalX=0 NormalY=0 NormalZ=1 AngleXU=0 Radius=0.5 StartAngle=0 EndAngle=1.5708
    g23: GeomPoint [constr] X=4.2 Y=-3.1 Z=0
    g24: ArcOfCircle CenterX=16.5 CenterY=-4 CenterZ=0 NormalX=0 NormalY=0 NormalZ=1 AngleXU=0 Radius=0.5 StartAngle=3e-16 EndAngle=1.5708
    g25: GeomPoint [constr] X=17 Y=-3.5 Z=0
    g26: ArcOfCircle CenterX=16.5 CenterY=-5.2 CenterZ=0 NormalX=0 NormalY=0 NormalZ=1 AngleXU=0 Radius=0.5 StartAngle=4.71239 EndAngle=6.28319
    g27: GeomPoint [constr] X=17 Y=-5.7 Z=0
    g28: ArcOfCircle CenterX=18.3 CenterY=-5.6 CenterZ=0 NormalX=0 NormalY=0 NormalZ=1 AngleXU=0 Radius=0.5 StartAngle=3.14159 EndAngle=4.71239
    g29: GeomPoint [constr] X=17.8 Y=-6.1 Z=0
    g30: ArcOfCircle CenterX=18.3 CenterY=-3.6 CenterZ=0 NormalX=0 NormalY=0 NormalZ=1 AngleXU=0 Radius=0.5 StartAngle=1.5708 EndAngle=3.14159
    g31: GeomPoint [constr] X=17.8 Y=-3.1 Z=0
    g32: LineSegment StartX=1.2 StartY=1.7 StartZ=0 EndX=1.2 EndY=-0.7 EndZ=0
    g33: LineSegment StartX=1.7 StartY=-1.2 StartZ=0 EndX=5.3 EndY=-1.2 EndZ=0
    g34: LineSegment StartX=5.8 StartY=-0.7 StartZ=0 EndX=5.8 EndY=1.7 EndZ=0
    g35: LineSegment StartX=5.3 StartY=2.2 StartZ=0 EndX=1.7 EndY=2.2 EndZ=0
    g36: LineSegment StartX=6.8 StartY=1.7 StartZ=0 EndX=6.8 EndY=-0.7 EndZ=0
    g37: LineSegment StartX=7.3 StartY=-1.2 StartZ=0 EndX=14.7 EndY=-1.2 EndZ=0
    g38: LineSegment StartX=15.2 StartY=-0.7 StartZ=0 EndX=15.2 EndY=1.7 EndZ=0
    g39: LineSegment StartX=14.7 StartY=2.2 StartZ=0 EndX=7.3 EndY=2.2 EndZ=0
    g40: LineSegment StartX=16.2 StartY=1.7 StartZ=0 EndX=16.2 EndY=-0.7 EndZ=0
    g41: LineSegment StartX=16.7 StartY=-1.2 StartZ=0 EndX=20.3 EndY=-1.2 EndZ=0
    g42: LineSegment StartX=20.8 StartY=-0.7 StartZ=0 EndX=20.8 EndY=1.7 EndZ=0
    g43: LineSegment StartX=20.3 StartY=2.2 StartZ=0 EndX=16.7 EndY=2.2 EndZ=0
    g44: ArcOfCircle CenterX=20.3 CenterY=1.7 CenterZ=0 NormalX=0 NormalY=0 NormalZ=1 AngleXU=0 Radius=0.5 StartAngle=0 EndAngle=1.5708
    g45: GeomPoint [constr] X=20.8 Y=2.2 Z=0
    g46: ArcOfCircle CenterX=16.7 CenterY=1.7 CenterZ=0 NormalX=0 NormalY=0 NormalZ=1 AngleXU=0 Radius=0.5 StartAngle=1.5708 EndAngle=3.14159
    g47: GeomPoint [constr] X=16.2 Y=2.2 Z=0
    g48: ArcOfCircle CenterX=16.7 CenterY=-0.7 CenterZ=0 NormalX=0 NormalY=0 NormalZ=1 AngleXU=0 Radius=0.5 StartAngle=3.14159 EndAngle=4.71239
    g49: GeomPoint [constr] X=16.2 Y=-1.2 Z=0
    g50: ArcOfCircle CenterX=20.3 CenterY=-0.7 CenterZ=0 NormalX=0 NormalY=0 NormalZ=1 AngleXU=0 Radius=0.5 StartAngle=4.71239 EndAngle=6.28319
    g51: GeomPoint [constr] X=20.8 Y=-1.2 Z=0
    g52: ArcOfCircle CenterX=14.7 CenterY=-0.7 CenterZ=0 NormalX=0 NormalY=0 NormalZ=1 AngleXU=0 Radius=0.5 StartAngle=4.71239 EndAngle=6.28319
    g53: GeomPoint [constr] X=15.2 Y=-1.2 Z=0
    g54: ArcOfCircle CenterX=14.7 CenterY=1.7 CenterZ=0 NormalX=0 NormalY=0 NormalZ=1 AngleXU=0 Radius=0.5 StartAngle=0 EndAngle=1.5708
    g55: GeomPoint [constr] X=15.2 Y=2.2 Z=0
    g56: ArcOfCircle CenterX=7.3 CenterY=-0.7 CenterZ=0 NormalX=0 NormalY=0 NormalZ=1 AngleXU=0 Radius=0.5 StartAngle=3.14159 EndAngle=4.71239
    g57: GeomPoint [constr] X=6.8 Y=-1.2 Z=0
    g58: ArcOfCircle CenterX=7.3 CenterY=1.7 CenterZ=0 NormalX=0 NormalY=0 NormalZ=1 AngleXU=0 Radius=0.5 StartAngle=1.5708 EndAngle=3.14159
    g59: GeomPoint [constr] X=6.8 Y=2.2 Z=0
    g60: ArcOfCircle CenterX=5.3 CenterY=1.7 CenterZ=0 NormalX=0 NormalY=0 NormalZ=1 AngleXU=0 Radius=0.5 StartAngle=1e-16 EndAngle=1.5708
    g61: GeomPoint [constr] X=5.8 Y=2.2 Z=0
    g62: ArcOfCircle CenterX=5.3 CenterY=-0.7 CenterZ=0 NormalX=0 NormalY=0 NormalZ=1 AngleXU=0 Radius=0.5 StartAngle=4.71239 EndAngle=6.28319
    g63: GeomPoint [constr] X=5.8 Y=-1.2 Z=0
    g64: ArcOfCircle CenterX=1.7 CenterY=-0.7 CenterZ=0 NormalX=0 NormalY=0 NormalZ=1 AngleXU=0 Radius=0.5 StartAngle=3.14159 EndAngle=4.71239
    g65: GeomPoint [constr] X=1.2 Y=-1.2 Z=0
    g66: ArcOfCircle CenterX=1.7 CenterY=1.7 CenterZ=0 NormalX=0 NormalY=0 NormalZ=1 AngleXU=0 Radius=0.5 StartAngle=1.5708 EndAngle=3.14159
    g67: GeomPoint [constr] X=1.2 Y=2.2 Z=0
  constraints (165):
    c: PointOnObject(g0,g-5)
    c: PointOnObject(g0,g-3)
    c: Horizontal(g0)
    c: Coincident(g1,g0)
    c: PointOnObject(g1,g-3)
    c: Coincident(g2,g1)
    c: Horizontal(g2)
    c: Vertical(g3)
    c: PointOnObject(g4,g-3)
    c: Coincident(g5,g4)
    c: PointOnObject(g5,g-3)
    c: Coincident(g6,g5)
    c: PointOnObject(g6,g-5)
    c: Horizontal(g6)
    c: Coincident(g7,g6)
    c: PointOnObject(g7,g-5)
    c: Coincident(g8,g7)
    c: Horizontal(g8)
    c: Vertical(g9)
    c: PointOnObject(g10,g-5)
    c: Horizontal(g10)
    c: Coincident(g11,g10)
    c: Coincident(g11,g0)
    c: Horizontal(g12)
    c: Vertical(g13)
    c: Horizontal(g14)
    c: PointOnObject(g17,g12)
    c: PointOnObject(g17,g13)
    c: Tangent(g12,g16) = -1.5708
    c: Tangent(g13,g16) = -1.5708
    c: PointOnObject(g19,g13)
    c: PointOnObject(g19,g14)
    c: Tangent(g13,g18) = -1.5708
    c: Tangent(g14,g18) = -1.5708
    c: PointOnObject(g21,g9)
    c: PointOnObject(g21,g10)
    c: Tangent(g9,g20) = 1.5708
    c: Tangent(g10,g20) = 1.5708
    c: PointOnObject(g23,g8)
    c: PointOnObject(g23,g9)
    c: Tangent(g8,g22) = 1.5708
    c: Tangent(g9,g22) = 1.5708
    c: PointOnObject(g25,g12)
    c: PointOnObject(g25,g15)
    c: Tangent(g12,g24) = -1.5708
    c: Tangent(g15,g24) = -1.5708
    c: PointOnObject(g27,g14)
    c: PointOnObject(g27,g15)
    c: Tangent(g14,g26) = -1.5708
    c: Tangent(g15,g26) = -1.5708
    c: PointOnObject(g29,g2)
    c: PointOnObject(g29,g3)
    c: Tangent(g2,g28) = 1.5708
    c: Tangent(g3,g28) = 1.5708
    c: PointOnObject(g31,g3)
    c: PointOnObject(g31,g4)
    c: Tangent(g3,g30) = 1.5708
    c: Tangent(g4,g30) = 1.5708
    c: Radius(g24) = 0.5
    c: Radius(g26) = 0.5
    c: Radius(g30) = 0.5
    c: Radius(g28) = 0.5
    c: Radius(g22) = 0.5
    c: Radius(g20) = 0.5
    c: Radius(g18) = 0.5
    c: Radius(g16) = 0.5
    c: DistanceY(g-7,g0) = 4
    c: DistanceY(g0,g5) = 4.8
    c: DistanceY(g0,g1) = 0.9
    c: DistanceY(g4,g5) = 0.9
    c: DistanceY(g7,g6) = 0.9
    c: DistanceY(g0,g10) = 0.9
    c: DistanceX(g7,g9) = 4
    c: DistanceX(g3,g4) = 4
    c: Horizontal(g4)
    c: Vertical(g15)
    c: DistanceY(g14,g12) = 2.2
    c: DistanceX(g12,g12) = 11
    c: DistanceY(g12,g6) = 1.3
    c: DistanceX(g-5,g-3) = 21.6
    c: DistanceX(g9,g13) = 0.8
    c: Vertical(g32)
    c: Vertical(g34)
    c: Horizontal(g33)
    c: Horizontal(g35)
    c: Vertical(g36)
    c: Vertical(g38)
    c: Horizontal(g37)
    c: Horizontal(g39)
    c: Vertical(g40)
    c: Vertical(g42)
    c: Horizontal(g41)
    c: Horizontal(g43)
    c: PointOnObject(g45,g42)
    c: PointOnObject(g45,g43)
    c: Tangent(g42,g44) = -1.5708
    c: Tangent(g43,g44) = -1.5708
    c: PointOnObject(g47,g40)
    c: PointOnObject(g47,g43)
    c: Tangent(g40,g46) = -1.5708
    c: Tangent(g43,g46) = -1.5708
    c: PointOnObject(g49,g40)
    c: PointOnObject(g49,g41)
    c: Tangent(g40,g48) = -1.5708
    c: Tangent(g41,g48) = -1.5708
    c: PointOnObject(g51,g41)
    c: PointOnObject(g51,g42)
    c: Tangent(g41,g50) = -1.5708
    c: Tangent(g42,g50) = -1.5708
    c: PointOnObject(g53,g37)
    c: PointOnObject(g53,g38)
    c: Tangent(g37,g52) = -1.5708
    c: Tangent(g38,g52) = -1.5708
    c: PointOnObject(g55,g38)
    c: PointOnObject(g55,g39)
    c: Tangent(g38,g54) = -1.5708
    c: Tangent(g39,g54) = -1.5708
    c: PointOnObject(g57,g36)
    c: PointOnObject(g57,g37)
    c: Tangent(g36,g56) = -1.5708
    c: Tangent(g37,g56) = -1.5708
    c: PointOnObject(g59,g36)
    c: PointOnObject(g59,g39)
    c: Tangent(g36,g58) = -1.5708
    c: Tangent(g39,g58) = -1.5708
    c: PointOnObject(g61,g34)
    c: PointOnObject(g61,g35)
    c: Tangent(g34,g60) = -1.5708
    c: Tangent(g35,g60) = -1.5708
    c: PointOnObject(g63,g33)
    c: PointOnObject(g63,g34)
    c: Tangent(g33,g62) = -1.5708
    c: Tangent(g34,g62) = -1.5708
    c: PointOnObject(g65,g32)
    c: PointOnObject(g65,g33)
    c: Tangent(g32,g64) = -1.5708
    c: Tangent(g33,g64) = -1.5708
    c: PointOnObject(g67,g32)
    c: PointOnObject(g67,g35)
    c: Tangent(g32,g66) = -1.5708
    c: Tangent(g35,g66) = -1.5708
    c: DistanceX(g34,g36) = 1
    c: DistanceX(g-5,g32) = 1
    c: DistanceX(g38,g40) = 1
    c: DistanceX(g42,g-3) = 1
    c: Radius(g58) = 0.5
    c: Radius(g54) = 0.5
    c: Radius(g52) = 0.5
    c: Radius(g56) = 0.5
    c: Radius(g48) = 0.5
    c: Radius(g46) = 0.5
    c: Radius(g44) = 0.5
    c: Radius(g50) = 0.5
    c: Radius(g60) = 0.5
    c: Radius(g62) = 0.5
    c: Radius(g64) = 0.5
    c: Radius(g66) = 0.5
    c: DistanceY(g35,g-4) = 2
    c: DistanceY(g6,g33) = 1
    c: DistanceY(g39,g-4) = 2
    c: DistanceY(g6,g37) = 1
    c: DistanceY(g43,g-4) = 2
    c: DistanceY(g5,g41) = 1
    c: DistanceX(g32,g34) = 4.6
    c: DistanceX(g40,g42) = 4.6
FEATURE [PartDesign::Pocket] Pocket087
  BaseFeature = -> Fillet017
  Direction = (0,1,-4.2e-15)
  Length = 0.5
  Length2 = 5
  Profile = -> Sketch261
  ReferenceAxis = -> Sketch261 [N_Axis]
  Refine = true
  Suppressed = false
  Type = 0
FEATURE [PartDesign::Fillet] Fillet018
  Base = -> Pocket087 [Edge68,Edge67,Edge65]
  BaseFeature = -> Pocket087
  Radius = 0.5
  Refine = true
  SupportTransform = false
  Suppressed = false
  UseAllEdges = false
FEATURE [Sketcher::SketchObject] Sketch262
  ArcFitTolerance = 1e-06
  AttachmentSupport = -> [Fillet018]
  ExternalGeometry = -> [Fillet018]
  FullyConstrained = true
  MakeInternals = false
  MapMode = 5
  Placement = pos=(0,-81.55,4.061e-13) rot=(1,0,0;1.5708rad)
  sketch-geometry (36):
    g0: LineSegment StartX=1.2 StartY=1.5 StartZ=0 EndX=1.2 EndY=1.3 EndZ=0
    g1: LineSegment StartX=1.2 StartY=1.3 StartZ=0 EndX=5.8 EndY=1.3 EndZ=0
    g2: LineSegment StartX=5.8 StartY=1.3 StartZ=0 EndX=5.8 EndY=1.5 EndZ=0
    g3: LineSegment StartX=5.8 StartY=1.5 StartZ=0 EndX=1.2 EndY=1.5 EndZ=0
    g4: LineSegment StartX=1.2 StartY=0.6 StartZ=0 EndX=1.2 EndY=0.4 EndZ=0
    g5: LineSegment StartX=1.2 StartY=0.4 StartZ=0 EndX=5.8 EndY=0.4 EndZ=0
    g6: LineSegment StartX=5.8 StartY=0.4 StartZ=0 EndX=5.8 EndY=0.6 EndZ=0
    g7: LineSegment StartX=5.8 StartY=0.6 StartZ=0 EndX=1.2 EndY=0.6 EndZ=0
    g8: LineSegment StartX=1.2 StartY=-0.3 StartZ=0 EndX=1.2 EndY=-0.5 EndZ=0
    g9: LineSegment StartX=1.2 StartY=-0.5 StartZ=0 EndX=5.8 EndY=-0.5 EndZ=0
    g10: LineSegment StartX=5.8 StartY=-0.5 StartZ=0 EndX=5.8 EndY=-0.3 EndZ=0
    g11: LineSegment StartX=5.8 StartY=-0.3 StartZ=0 EndX=1.2 EndY=-0.3 EndZ=0
    g12: LineSegment StartX=15.2 StartY=1.5 StartZ=0 EndX=6.8 EndY=1.5 EndZ=0
    g13: LineSegment StartX=6.8 StartY=1.5 StartZ=0 EndX=6.8 EndY=1.3 EndZ=0
    g14: LineSegment StartX=6.8 StartY=1.3 StartZ=0 EndX=15.2 EndY=1.3 EndZ=0
    g15: LineSegment StartX=15.2 StartY=1.3 StartZ=0 EndX=15.2 EndY=1.5 EndZ=0
    g16: LineSegment StartX=15.2 StartY=0.6 StartZ=0 EndX=6.8 EndY=0.6 EndZ=0
    g17: LineSegment StartX=6.8 StartY=0.6 StartZ=0 EndX=6.8 EndY=0.4 EndZ=0
    g18: LineSegment StartX=6.8 StartY=0.4 StartZ=0 EndX=15.2 EndY=0.4 EndZ=0
    g19: LineSegment StartX=15.2 StartY=0.4 StartZ=0 EndX=15.2 EndY=0.6 EndZ=0
    g20: LineSegment StartX=15.2 StartY=-0.3 StartZ=0 EndX=6.8 EndY=-0.3 EndZ=0
    g21: LineSegment StartX=6.8 StartY=-0.3 StartZ=0 EndX=6.8 EndY=-0.5 EndZ=0
    g22: LineSegment StartX=6.8 StartY=-0.5 StartZ=0 EndX=15.2 EndY=-0.5 EndZ=0
    g23: LineSegment StartX=15.2 StartY=-0.5 StartZ=0 EndX=15.2 EndY=-0.3 EndZ=0
    g24: LineSegment StartX=20.8 StartY=1.5 StartZ=0 EndX=16.2 EndY=1.5 EndZ=0
    g25: LineSegment StartX=16.2 StartY=1.5 StartZ=0 EndX=16.2 EndY=1.3 EndZ=0
    g26: LineSegment StartX=16.2 StartY=1.3 StartZ=0 EndX=20.8 EndY=1.3 EndZ=0
    g27: LineSegment StartX=20.8 StartY=1.3 StartZ=0 EndX=20.8 EndY=1.5 EndZ=0
    g28: LineSegment StartX=20.8 StartY=0.6 StartZ=0 EndX=16.2 EndY=0.6 EndZ=0
    g29: LineSegment StartX=16.2 StartY=0.6 StartZ=0 EndX=16.2 EndY=0.4 EndZ=0
    g30: LineSegment StartX=16.2 StartY=0.4 StartZ=0 EndX=20.8 EndY=0.4 EndZ=0
    g31: LineSegment StartX=20.8 StartY=0.4 StartZ=0 EndX=20.8 EndY=0.6 EndZ=0
    g32: LineSegment StartX=20.8 StartY=-0.3 StartZ=0 EndX=16.2 EndY=-0.3 EndZ=0
    g33: LineSegment StartX=16.2 StartY=-0.3 StartZ=0 EndX=16.2 EndY=-0.5 EndZ=0
    g34: LineSegment StartX=16.2 StartY=-0.5 StartZ=0 EndX=20.8 EndY=-0.5 EndZ=0
    g35: LineSegment StartX=20.8 StartY=-0.5 StartZ=0 EndX=20.8 EndY=-0.3 EndZ=0
  constraints (110):
    c: Coincident(g0,g1)
    c: Coincident(g1,g2)
    c: Coincident(g2,g3)
    c: Coincident(g3,g0)
    c: Vertical(g0)
    c: Vertical(g2)
    c: Horizontal(g1)
    c: Horizontal(g3)
    c: PointOnObject(g0,g-3)
    c: PointOnObject(g1,g-4)
    c: Coincident(g4,g5)
    c: Coincident(g5,g6)
    c: Coincident(g6,g7)
    c: Coincident(g7,g4)
    c: Vertical(g4)
    c: Vertical(g6)
    c: Horizontal(g5)
    c: Horizontal(g7)
    c: PointOnObject(g4,g-3)
    c: Coincident(g8,g9)
    c: Coincident(g9,g10)
    c: Coincident(g10,g11)
    c: Coincident(g11,g8)
    c: Vertical(g8)
    c: Vertical(g10)
    c: Horizontal(g9)
    c: Horizontal(g11)
    c: PointOnObject(g8,g-3)
    c: PointOnObject(g9,g-4)
    c: DistanceY(g-10,g-9) = 3.4
    c: DistanceY(g0,g-9) = 0.7
    c: DistanceY(g0,g0) = 0.2
    c: DistanceY(g4,g4) = 0.2
    c: DistanceY(g8,g8) = 0.2
    c: DistanceY(g4,g0) = 0.7
    c: DistanceY(g8,g4) = 0.7
    c: PointOnObject(g6,g-4)
    c: Coincident(g12,g13)
    c: Coincident(g13,g14)
    c: Coincident(g14,g15)
    c: Coincident(g15,g12)
    c: Horizontal(g12)
    c: Horizontal(g14)
    c: Vertical(g13)
    c: Vertical(g15)
    c: PointOnObject(g12,g-6)
    c: Coincident(g16,g17)
    c: Coincident(g17,g18)
    c: Coincident(g18,g19)
    c: Coincident(g19,g16)
    c: Horizontal(g16)
    c: Horizontal(g18)
    c: Vertical(g17)
    c: Vertical(g19)
    c: Coincident(g20,g21)
    c: Coincident(g21,g22)
    c: Coincident(g22,g23)
    c: Coincident(g23,g20)
    c: Horizontal(g20)
    c: Horizontal(g22)
    c: Vertical(g21)
    c: Vertical(g23)
    c: PointOnObject(g20,g-6)
    c: PointOnObject(g12,g-11)
    c: PointOnObject(g16,g-11)
    c: PointOnObject(g20,g-11)
    c: DistanceY(g21,g21) = 0.2
    c: DistanceY(g17,g17) = 0.2
    c: DistanceY(g13,g13) = 0.2
    c: DistanceY(g12,g-13) = 0.7
    c: DistanceY(g16,g13) = 0.7
    c: DistanceY(g20,g17) = 0.7
    c: PointOnObject(g16,g-6)
    c: Coincident(g24,g25)
    c: Coincident(g25,g26)
    c: Coincident(g26,g27)
    c: Coincident(g27,g24)
    c: Horizontal(g24)
    c: Horizontal(g26)
    c: Vertical(g25)
    c: Vertical(g27)
    c: PointOnObject(g24,g-8)
    c: Coincident(g28,g29)
    c: Coincident(g29,g30)
    c: Coincident(g30,g31)
    c: Coincident(g31,g28)
    c: Horizontal(g28)
    c: Horizontal(g30)
    c: Vertical(g29)
    c: Vertical(g31)
    c: PointOnObject(g28,g-8)
    c: Coincident(g32,g33)
    c: Coincident(g33,g34)
    c: Coincident(g34,g35)
    c: Coincident(g35,g32)
    c: Horizontal(g32)
    c: Horizontal(g34)
    c: Vertical(g33)
    c: Vertical(g35)
    c: PointOnObject(g32,g-8)
    c: PointOnObject(g32,g-12)
    c: PointOnObject(g28,g-12)
    c: PointOnObject(g24,g-12)
    c: DistanceY(g25,g25) = 0.2
    c: DistanceY(g29,g29) = 0.2
    c: DistanceY(g-12,g-12) = 20000
    c: DistanceY(g33,g33) = 0.2
    c: DistanceY(g24,g-14) = 0.7
    c: DistanceY(g28,g25) = 0.7
    c: DistanceY(g32,g29) = 0.7
FEATURE [PartDesign::Pad] Pad202
  BaseFeature = -> Fillet018
  Direction = (0,-1,4.9e-15)
  Length = 0.25
  Length2 = 10
  Profile = -> Sketch262
  ReferenceAxis = -> Sketch262 [N_Axis]
  Refine = true
  Suppressed = false
  Type = 0
FEATURE [PartDesign::Fillet] Fillet019
  Base = -> Pad202 [Edge109,Edge55,Edge56,Edge57,Edge59,Edge52,Edge7,Edge8]
  BaseFeature = -> Pad202
  Radius = 0.5
  Refine = true
  SupportTransform = false
  Suppressed = false
  UseAllEdges = false
FEATURE [PartDesign::Pocket] Pocket228
  BaseFeature = -> Fillet019
  Direction = (0,-4e-15,-1)
  Length = 0.2
  Length2 = 5
  Profile = -> Fillet019 [Face15]
  Refine = true
  Suppressed = false
  Type = 0
FEATURE [PartDesign::Chamfer] Chamfer001
  Angle = 45
  Base = -> Pocket228 [Edge164]
  BaseFeature = -> Pocket228
  ChamferType = 0
  FlipDirection = false
  Refine = true
  Size = 0.3
  Size2 = 1
  SupportTransform = false
  Suppressed = false
  UseAllEdges = false
FEATURE [PartDesign::Body] Body027  label="Grill"
  AllowCompound = false
  Group = -> [Binder015,Sketch256,Pad172,Sketch257,Pad173,Sketch258,Pocket086,Sketch259,Pad174,Sketch260,Pad175,Pad201,Fillet017,Sketch261,Pocket087,Fillet018,Sketch262,Pad202,Fillet019,Pocket228,Chamfer001]
  Origin = -> Origin029
  Placement = pos=(33,38,0) rot=(0,0,1;0rad)
  Tip = -> Chamfer001
COMPONENT P16 — recipe-attached ("Pre_Right_Wheel Holder", modeled in this document).
Construction recipe (the document's own serialized feature program — sketch geometry with constraints, then the solid features built on it; lengths are millimeters unless a unit is written):

FEATURE [PartDesign::SubShapeBinder] Binder017
  BindCopyOnChange = 0
  BindMode = 2
  ClaimChildren = false
  Context = -> Body028 [Binder017.]
  Fuse = false
  MakeFace = true
  OffsetFill = false
  OffsetIntersection = false
  OffsetJoinType = 0
  OffsetOpenResult = false
  PartialLoad = false
  Refine = true
  Relative = true
  _Version = 2
FEATURE [Sketcher::SketchObject] Sketch273
  ArcFitTolerance = 1e-06
  AttachmentSupport = -> [Binder017]
  ExternalGeometry = -> [Binder017]
  FullyConstrained = true
  MakeInternals = false
  MapMode = 5
  Placement = pos=(0.2,0,1.9e-15) rot=(0.57735,-0.57735,-0.57735;2.0944rad)
  sketch-geometry (6):
    g0: LineSegment StartX=77.35 StartY=0.7 StartZ=0 EndX=56.15 EndY=0.7 EndZ=0
    g1: LineSegment StartX=56.15 StartY=0.7 StartZ=0 EndX=56.15 EndY=-11 EndZ=0
    g2: LineSegment StartX=56.15 StartY=-11 StartZ=0 EndX=73.85 EndY=-11 EndZ=0
    g3: LineSegment StartX=73.85 StartY=-11 StartZ=0 EndX=73.85 EndY=-3.1 EndZ=0
    g4: LineSegment StartX=73.85 StartY=-3.1 StartZ=0 EndX=77.35 EndY=-3.1 EndZ=0
    g5: LineSegment StartX=77.35 StartY=-3.1 StartZ=0 EndX=77.35 EndY=0.7 EndZ=0
  constraints (18):
    c: Horizontal(g0)
    c: Coincident(g1,g0)
    c: Vertical(g1)
    c: Coincident(g2,g1)
    c: PointOnObject(g2,g-4)
    c: Horizontal(g2)
    c: Coincident(g3,g2)
    c: Vertical(g3)
    c: Coincident(g4,g3)
    c: Horizontal(g4)
    c: Coincident(g5,g4)
    c: Coincident(g5,g0)
    c: Vertical(g5)
    c: DistanceY(g1,g1) = 11.7
    c: DistanceY(g5,g5) = 3.8
    c: DistanceX(g4,g4) = 3.5
    c: DistanceX(g0,g0) = 21.2
    c: DistanceX(g4,g-4) = 1.7
FEATURE [PartDesign::Pad] Pad185
  Direction = (-1,0,-9.3e-15)
  Length = 2
  Length2 = 10
  Profile = -> Sketch273
  ReferenceAxis = -> Sketch273 [N_Axis]
  Refine = true
  Suppressed = false
  Type = 0
FEATURE [Sketcher::SketchObject] Sketch274
  ArcFitTolerance = 1e-06
  AttachmentSupport = -> [Pad185]
  ExternalGeometry = -> [Pad185]
  FullyConstrained = true
  MakeInternals = false
  MapMode = 5
  Placement = pos=(-1.8,0,-1.68e-14) rot=(0.57735,-0.57735,-0.57735;2.0944rad)
  sketch-geometry (12):
    g0: LineSegment StartX=62.15 StartY=0.7 StartZ=0 EndX=62.15 EndY=-1.3 EndZ=0
    g1: LineSegment StartX=62.15 StartY=-1.3 StartZ=0 EndX=68.25 EndY=-1.3 EndZ=0
    g2: LineSegment StartX=68.25 StartY=-1.3 StartZ=0 EndX=68.25 EndY=0.7 EndZ=0
    g3: LineSegment StartX=68.25 StartY=0.7 StartZ=0 EndX=62.15 EndY=0.7 EndZ=0
    g4: LineSegment StartX=73.85 StartY=-11 StartZ=0 EndX=73.85 EndY=-7.1 EndZ=0
    g5: LineSegment StartX=73.85 StartY=-7.1 StartZ=0 EndX=71.85 EndY=-7.1 EndZ=0
    g6: LineSegment StartX=71.85 StartY=-7.1 StartZ=0 EndX=71.85 EndY=-11 EndZ=0
    g7: LineSegment StartX=71.85 StartY=-11 StartZ=0 EndX=73.85 EndY=-11 EndZ=0
    g8: LineSegment StartX=56.15 StartY=-11 StartZ=0 EndX=58.15 EndY=-11 EndZ=0
    g9: LineSegment StartX=58.15 StartY=-11 StartZ=0 EndX=58.15 EndY=-7.1 EndZ=0
    g10: LineSegment StartX=58.15 StartY=-7.1 StartZ=0 EndX=56.15 EndY=-7.1 EndZ=0
    g11: LineSegment StartX=56.15 StartY=-7.1 StartZ=0 EndX=56.15 EndY=-11 EndZ=0
  constraints (34):
    c: Coincident(g0,g1)
    c: Coincident(g1,g2)
    c: Coincident(g2,g3)
    c: Coincident(g3,g0)
    c: Vertical(g0)
    c: Vertical(g2)
    c: Horizontal(g1)
    c: Horizontal(g3)
    c: PointOnObject(g0,g-5)
    c: Coincident(g4,g5)
    c: Coincident(g5,g6)
    c: Coincident(g6,g7)
    c: Coincident(g7,g4)
    c: Vertical(g4)
    c: Vertical(g6)
    c: Horizontal(g5)
    c: Horizontal(g7)
    c: Coincident(g4,g-6)
    c: Coincident(g8,g9)
    c: Coincident(g9,g10)
    c: Coincident(g10,g11)
    c: Coincident(g11,g8)
    c: Horizontal(g8)
    c: Horizontal(g10)
    c: Vertical(g9)
    c: Vertical(g11)
    c: Coincident(g8,g-6)
    c: DistanceX(g10,g10) = 2
    c: DistanceX(g5,g5) = 2
    c: DistanceY(g2,g2) = 2
    c: DistanceY(g9,g9) = 3.9
    c: DistanceY(g6,g6) = 3.9
    c: DistanceX(g1,g1) = 6.1
    c: DistanceX(g-5,g0) = 6
FEATURE [PartDesign::Pad] Pad186
  BaseFeature = -> Pad185
  Direction = (-1,0,-9.3e-15)
  Length = 2
  Length2 = 10
  Profile = -> Sketch274
  ReferenceAxis = -> Sketch274 [N_Axis]
  Refine = true
  Suppressed = false
  Type = 0
FEATURE [Sketcher::SketchObject] Sketch275
  ArcFitTolerance = 1e-06
  AttachmentSupport = -> [Pad186]
  ExternalGeometry = -> [Pad186]
  FullyConstrained = true
  MakeInternals = false
  MapMode = 5
  Placement = pos=(-3.8,0,-3.54e-14) rot=(0.57735,-0.57735,-0.57735;2.0944rad)
  sketch-geometry (12):
    g0: LineSegment StartX=58.15 StartY=-7.1 StartZ=0 EndX=54.15 EndY=-7.1 EndZ=0
    g1: LineSegment StartX=54.15 StartY=-7.1 StartZ=0 EndX=54.15 EndY=-11 EndZ=0
    g2: LineSegment StartX=54.15 StartY=-11 StartZ=0 EndX=58.15 EndY=-11 EndZ=0
    g3: LineSegment StartX=58.15 StartY=-11 StartZ=0 EndX=58.15 EndY=-7.1 EndZ=0
    g4: LineSegment StartX=71.85 StartY=-7.1 StartZ=0 EndX=71.85 EndY=-11 EndZ=0
    g5: LineSegment StartX=71.85 StartY=-11 StartZ=0 EndX=75.85 EndY=-11 EndZ=0
    g6: LineSegment StartX=75.85 StartY=-11 StartZ=0 EndX=75.85 EndY=-7.1 EndZ=0
    g7: LineSegment StartX=75.85 StartY=-7.1 StartZ=0 EndX=71.85 EndY=-7.1 EndZ=0
    g8: LineSegment StartX=68.25 StartY=-1.3 StartZ=0 EndX=68.25 EndY=2.2 EndZ=0
    g9: LineSegment StartX=68.25 StartY=2.2 StartZ=0 EndX=62.15 EndY=2.2 EndZ=0
    g10: LineSegment StartX=62.15 StartY=2.2 StartZ=0 EndX=62.15 EndY=-1.3 EndZ=0
    g11: LineSegment StartX=62.15 StartY=-1.3 StartZ=0 EndX=68.25 EndY=-1.3 EndZ=0
  constraints (31):
    c: Coincident(g0,g1)
    c: Coincident(g1,g2)
    c: Coincident(g2,g3)
    c: Coincident(g3,g0)
    c: Horizontal(g0)
    c: Horizontal(g2)
    c: Vertical(g1)
    c: Coincident(g0,g-7)
    c: Coincident(g4,g5)
    c: Coincident(g5,g6)
    c: Coincident(g6,g7)
    c: Coincident(g7,g4)
    c: Vertical(g6)
    c: Horizontal(g5)
    c: Horizontal(g7)
    c: Coincident(g4,g-10)
    c: Coincident(g8,g9)
    c: Coincident(g9,g10)
    c: Coincident(g10,g11)
    c: Coincident(g11,g8)
    c: Vertical(g8)
    c: Vertical(g10)
    c: Horizontal(g9)
    c: Horizontal(g11)
    c: Coincident(g8,g-4)
    c: PointOnObject(g-5,g10)
    c: Coincident(g-11,g4)
    c: Coincident(g2,g-8)
    c: DistanceX(g0,g0) = 4
    c: DistanceX(g7,g7) = 4
    c: DistanceY(g8,g8) = 3.5
FEATURE [PartDesign::Pad] Pad187
  BaseFeature = -> Pad186
  Direction = (-1,0,-9.3e-15)
  Length = 2
  Length2 = 10
  Profile = -> Sketch275
  ReferenceAxis = -> Sketch275 [N_Axis]
  Refine = true
  Suppressed = false
  Type = 0
FEATURE [Sketcher::SketchObject] Sketch276
  ArcFitTolerance = 1e-06
  AttachmentSupport = -> [Pad187]
  ExternalGeometry = -> [Pad187]
  FullyConstrained = true
  MakeInternals = false
  MapMode = 5
  Placement = pos=(-1.8,0,-1.68e-14) rot=(0.57735,-0.57735,-0.57735;2.0944rad)
  sketch-geometry (1):
    g0: Circle CenterX=65 CenterY=-8 CenterZ=0 NormalX=0 NormalY=0 NormalZ=1 AngleXU=0 Radius=0.75
  constraints (4):
    c: DistanceX(g-3,g-3) = 13.7
    c: Diameter(g0) = 1.5
    c: DistanceX(g-3,g0) = 6.85
    c: DistanceY(g-3,g0) = 3
FEATURE [PartDesign::Pocket] Pocket131
  BaseFeature = -> Pad187
  Direction = (1,0,9.3e-15)
  Length = 2
  Length2 = 5
  Profile = -> Sketch276
  ReferenceAxis = -> Sketch276 [N_Axis]
  Refine = true
  Suppressed = false
  Type = 0
FEATURE [Sketcher::SketchObject] Sketch277
  ArcFitTolerance = 1e-06
  AttachmentSupport = -> [Pocket131]
  ExternalGeometry = -> [Pocket131]
  FullyConstrained = true
  MakeInternals = false
  MapMode = 5
  Placement = pos=(-3.8,0,-3.54e-14) rot=(0.57735,0.57735,0.57735;2.0944rad)
  sketch-geometry (8):
    g0: LineSegment StartX=-75.85 StartY=-8.55 StartZ=0 EndX=-75.85 EndY=-9.55 EndZ=0
    g1: LineSegment StartX=-75.85 StartY=-9.55 StartZ=0 EndX=-73.85 EndY=-9.55 EndZ=0
    g2: LineSegment StartX=-73.85 StartY=-9.55 StartZ=0 EndX=-73.85 EndY=-8.55 EndZ=0
    g3: LineSegment StartX=-73.85 StartY=-8.55 StartZ=0 EndX=-75.85 EndY=-8.55 EndZ=0
    g4: LineSegment StartX=-54.15 StartY=-8.55 StartZ=0 EndX=-56.15 EndY=-8.55 EndZ=0
    g5: LineSegment StartX=-56.15 StartY=-8.55 StartZ=0 EndX=-56.15 EndY=-9.55 EndZ=0
    g6: LineSegment StartX=-56.15 StartY=-9.55 StartZ=0 EndX=-54.15 EndY=-9.55 EndZ=0
    g7: LineSegment StartX=-54.15 StartY=-9.55 StartZ=0 EndX=-54.15 EndY=-8.55 EndZ=0
  constraints (25):
    c: Coincident(g0,g1)
    c: Coincident(g1,g2)
    c: Coincident(g2,g3)
    c: Coincident(g3,g0)
    c: Vertical(g0)
    c: Vertical(g2)
    c: Horizontal(g1)
    c: Horizontal(g3)
    c: PointOnObject(g0,g-10)
    c: PointOnObject(g1,g-8)
    c: Coincident(g4,g5)
    c: Coincident(g5,g6)
    c: Coincident(g6,g7)
    c: Coincident(g7,g4)
    c: Horizontal(g4)
    c: Horizontal(g6)
    c: Vertical(g5)
    c: Vertical(g7)
    c: PointOnObject(g4,g-4)
    c: PointOnObject(g5,g-3)
    c: DistanceY(g7,g7) = 1
    c: DistanceY(g0,g0) = 1
    c: DistanceY(g-10,g-10) = 3.9
    c: DistanceY(g0,g-10) = 1.45
    c: DistanceY(g4,g-5) = 1.45
FEATURE [PartDesign::Pad] Pad188
  BaseFeature = -> Pocket131
  Direction = (1,0,9.3e-15)
  Length = 0.25
  Length2 = 10
  Profile = -> Sketch277
  ReferenceAxis = -> Sketch277 [N_Axis]
  Refine = true
  Suppressed = false
  Type = 0
FEATURE [PartDesign::Fillet] Fillet021
  Base = -> Pad188 [Edge76,Edge78,Edge85,Edge86]
  BaseFeature = -> Pad188
  Radius = 0.24
  Refine = true
  SupportTransform = false
  Suppressed = false
  UseAllEdges = false
FEATURE [Sketcher::SketchObject] Sketch278
  ArcFitTolerance = 1e-06
  AttachmentSupport = -> [Fillet021]
  ExternalGeometry = -> [Fillet021]
  FullyConstrained = true
  MakeInternals = false
  MapMode = 5
  Placement = pos=(0.2,0,1.9e-15) rot=(0.57735,0.57735,0.57735;2.0944rad)
  sketch-geometry (2):
    g0: Circle CenterX=-58.32 CenterY=-5.4 CenterZ=0 NormalX=0 NormalY=0 NormalZ=1 AngleXU=0 Radius=1.1
    g1: Circle CenterX=-75.55 CenterY=-0.67 CenterZ=0 NormalX=0 NormalY=0 NormalZ=1 AngleXU=0 Radius=1
  constraints (7):
    c: Diameter(g1) = 2
    c: Diameter(g0) = 2.2
    c: DistanceX(g0,g-5) = 2.17
    c: DistanceY(g0,g-4) = 6.1
    c: DistanceX(g-6,g1) = 1.8
    c: DistanceY(g-6,g-6) = 3.8
    c: DistanceY(g1,g-6) = 1.37
FEATURE [PartDesign::Pad] Pad189
  BaseFeature = -> Fillet021
  Direction = (1,0,9.3e-15)
  Length = 2
  Length2 = 10
  Profile = -> Sketch278 [Edge2]
  ReferenceAxis = -> Sketch278 [N_Axis]
  Refine = true
  Suppressed = false
  Type = 0
FEATURE [PartDesign::Pad] Pad190
  BaseFeature = -> Pad189
  Direction = (1,0,9.3e-15)
  Length = 0.95
  Length2 = 10
  Profile = -> Sketch278 [Edge1]
  ReferenceAxis = -> Sketch278 [N_Axis]
  Refine = true
  Suppressed = false
  Type = 0
FEATURE [Sketcher::SketchObject] Sketch279
  ArcFitTolerance = 1e-06
  AttachmentSupport = -> [Pad190]
  ExternalGeometry = -> [Pad190]
  FullyConstrained = true
  MakeInternals = false
  MapMode = 5
  Placement = pos=(-3.55,0,-3.31e-14) rot=(0.57735,0.57735,0.57735;2.0944rad)
  sketch-geometry (8):
    g0: LineSegment StartX=-73.85 StartY=-8.39 StartZ=0 EndX=-75.85 EndY=-8.39 EndZ=0
    g1: LineSegment StartX=-75.85 StartY=-8.39 StartZ=0 EndX=-75.85 EndY=-9.71 EndZ=0
    g2: LineSegment StartX=-75.85 StartY=-9.71 StartZ=0 EndX=-73.85 EndY=-9.71 EndZ=0
    g3: LineSegment StartX=-73.85 StartY=-9.71 StartZ=0 EndX=-73.85 EndY=-8.39 EndZ=0
    g4: LineSegment StartX=-56.15 StartY=-8.39 StartZ=0 EndX=-56.15 EndY=-9.71 EndZ=0
    g5: LineSegment StartX=-56.15 StartY=-9.71 StartZ=0 EndX=-54.15 EndY=-9.71 EndZ=0
    g6: LineSegment StartX=-54.15 StartY=-9.71 StartZ=0 EndX=-54.15 EndY=-8.39 EndZ=0
    g7: LineSegment StartX=-54.15 StartY=-8.39 StartZ=0 EndX=-56.15 EndY=-8.39 EndZ=0
  constraints (24):
    c: Coincident(g0,g1)
    c: Coincident(g1,g2)
    c: Coincident(g2,g3)
    c: Coincident(g3,g0)
    c: Horizontal(g0)
    c: Horizontal(g2)
    c: Vertical(g1)
    c: Vertical(g3)
    c: PointOnObject(g-8,g3)
    c: PointOnObject(g-10,g1)
    c: DistanceY(g-10,g0) = 0.4
    c: DistanceY(g1,g-10) = 0.4
    c: Coincident(g4,g5)
    c: Coincident(g5,g6)
    c: Coincident(g6,g7)
    c: Coincident(g7,g4)
    c: Vertical(g4)
    c: Vertical(g6)
    c: Horizontal(g5)
    c: Horizontal(g7)
    c: PointOnObject(g-4,g4)
    c: PointOnObject(g-6,g6)
    c: DistanceY(g-6,g6) = 0.4
    c: DistanceY(g5,g-6) = 0.4
FEATURE [PartDesign::Pocket] Pocket132
  BaseFeature = -> Pad190
  Direction = (-1,0,-9.3e-15)
  Length = 0.1
  Length2 = 5
  Profile = -> Sketch279
  ReferenceAxis = -> Sketch279 [N_Axis]
  Refine = true
  Suppressed = false
  Type = 0
FEATURE [Sketcher::SketchObject] Sketch280
  ArcFitTolerance = 1e-06
  AttachmentSupport = -> [Pocket132]
  ExternalGeometry = -> [Pocket132]
  FullyConstrained = true
  MakeInternals = false
  MapMode = 5
  Placement = pos=(0.2,0,1.9e-15) rot=(0.57735,0.57735,0.57735;2.0944rad)
  sketch-geometry (6):
    g0: LineSegment StartX=-73.85 StartY=-3.1 StartZ=0 EndX=-71.35 EndY=-3.1 EndZ=0
    g1: LineSegment StartX=-70.35 StartY=-2.1 StartZ=0 EndX=-70.35 EndY=0.7 EndZ=0
    g2: LineSegment StartX=-70.35 StartY=0.7 StartZ=0 EndX=-73.85 EndY=0.7 EndZ=0
    g3: LineSegment StartX=-73.85 StartY=0.7 StartZ=0 EndX=-73.85 EndY=-3.1 EndZ=0
    g4: ArcOfCircle CenterX=-71.35 CenterY=-2.1 CenterZ=0 NormalX=0 NormalY=0 NormalZ=1 AngleXU=0 Radius=1 StartAngle=4.71239 EndAngle=6.28319
    g5: GeomPoint [constr] X=-70.35 Y=-3.1 Z=0
  constraints (15):
    c: Coincident(g1,g2)
    c: Coincident(g2,g3)
    c: Coincident(g3,g0)
    c: Horizontal(g0)
    c: Horizontal(g2)
    c: Vertical(g1)
    c: Vertical(g3)
    c: Coincident(g0,g-4)
    c: PointOnObject(g1,g-3)
    c: PointOnObject(g5,g0)
    c: PointOnObject(g5,g1)
    c: Tangent(g0,g4) = -1.5708
    c: Tangent(g1,g4) = -1.5708
    c: DistanceX(g2,g2) = 3.5
    c: Radius(g4) = 1
FEATURE [PartDesign::Pad] Pad191
  BaseFeature = -> Pocket132
  Direction = (1,0,9.3e-15)
  Length = 0.25
  Length2 = 10
  Profile = -> Sketch280
  ReferenceAxis = -> Sketch280 [N_Axis]
  Refine = true
  Suppressed = false
  Type = 0
FEATURE [Sketcher::SketchObject] Sketch313
  ArcFitTolerance = 1e-06
  AttachmentSupport = -> [Pad191]
  ExternalGeometry = -> [Pad191]
  FullyConstrained = true
  MakeInternals = false
  MapMode = 5
  Placement = pos=(-1.8,0,-1.68e-14) rot=(0.57735,-0.57735,-0.57735;2.0944rad)
  sketch-geometry (1):
    g0: Circle CenterX=65 CenterY=-8 CenterZ=0 NormalX=0 NormalY=0 NormalZ=1 AngleXU=0 Radius=0.8
  constraints (2):
    c: Coincident(g0,g-3)
    c: Radius(g0) = 0.8
FEATURE [PartDesign::Pocket] Pocket221
  BaseFeature = -> Pad191
  Direction = (1,0,9.3e-15)
  Length = 5
  Length2 = 5
  Profile = -> Sketch313
  ReferenceAxis = -> Sketch313 [N_Axis]
  Refine = true
  Suppressed = false
  Type = 0
FEATURE [PartDesign::Pad] Pad216
  BaseFeature = -> Pocket221
  Direction = (1,0,9.3e-15)
  Length = 0.05
  Length2 = 10
  Profile = -> Pocket221 [Face41]
  Refine = true
  Suppressed = false
  Type = 0
FEATURE [PartDesign::Body] Body028  label="Pre_Right_Wheel Holder"
  AllowCompound = false
  Group = -> [Binder017,Sketch273,Pad185,Sketch274,Pad186,Sketch275,Pad187,Sketch276,Pocket131,Sketch277,Pad188,Fillet021,Sketch278,Pad189,Pad190,Sketch279,Pocket132,Sketch280,Pad191,Sketch313,Pocket221,Pad216]
  Origin = -> Origin030
  Placement = pos=(-58,0,0) rot=(0,0,1;0rad)
  Tip = -> Pad216
COMPONENT P17 — recipe-attached ("Spring_Stop", modeled in this document).
Construction recipe (the document's own serialized feature program — sketch geometry with constraints, then the solid features built on it; lengths are millimeters unless a unit is written):

FEATURE [Sketcher::SketchObject] Sketch306
  ArcFitTolerance = 1e-06
  AttachmentSupport = -> [XZ_Plane031]
  FullyConstrained = false
  MakeInternals = false
  MapMode = 5
  Placement = pos=(0,0,0) rot=(1,0,0;1.5708rad)
  sketch-geometry (4):
    g0: LineSegment StartX=46.5745 StartY=12.8542 StartZ=0 EndX=41.5745 EndY=12.8542 EndZ=0
    g1: LineSegment StartX=41.5745 StartY=12.8542 StartZ=0 EndX=41.5745 EndY=10.8542 EndZ=0
    g2: LineSegment StartX=41.5745 StartY=10.8542 StartZ=0 EndX=46.5745 EndY=10.8542 EndZ=0
    g3: LineSegment StartX=46.5745 StartY=10.8542 StartZ=0 EndX=46.5745 EndY=12.8542 EndZ=0
  constraints (10):
    c: Coincident(g0,g1)
    c: Coincident(g1,g2)
    c: Coincident(g2,g3)
    c: Coincident(g3,g0)
    c: Horizontal(g0)
    c: Horizontal(g2)
    c: Vertical(g1)
    c: Vertical(g3)
    c: DistanceX(g0,g0) = 5
    c: DistanceY(g3,g3) = 2
FEATURE [PartDesign::Pad] Pad207
  Direction = (0,-1,2e-16)
  Length = 5
  Length2 = 10
  Placement = pos=(0,0,0) rot=(1,0,0;1.5708rad)
  Profile = -> Sketch306
  ReferenceAxis = -> Sketch306 [N_Axis]
  Refine = true
  Suppressed = false
  Type = 0
FEATURE [Sketcher::SketchObject] Sketch307
  ArcFitTolerance = 1e-06
  AttachmentSupport = -> [Pad207]
  ExternalGeometry = -> [Pad207]
  FullyConstrained = true
  MakeInternals = false
  MapMode = 5
  Placement = pos=(0,4.8e-15,10.8542) rot=(1,0,0;3.14159rad)
  sketch-geometry (1):
    g0: Circle CenterX=44.0745 CenterY=2.5 CenterZ=0 NormalX=0 NormalY=0 NormalZ=1 AngleXU=0 Radius=1
  constraints (2):
    c: Symmetric(g-3,g-4,g0)
    c: Radius(g0) = 1
FEATURE [PartDesign::Pocket] Pocket216
  BaseFeature = -> Pad207
  Direction = (0,0,1)
  Length = 5
  Length2 = 5
  Placement = pos=(0,0,0) rot=(1,0,0;1.5708rad)
  Profile = -> Sketch307
  ReferenceAxis = -> Sketch307 [N_Axis]
  Refine = true
  Suppressed = false
  Type = 0
FEATURE [Sketcher::SketchObject] Sketch308
  ArcFitTolerance = 1e-06
  AttachmentSupport = -> [Pocket216]
  ExternalGeometry = -> [Pocket216]
  FullyConstrained = true
  MakeInternals = false
  MapMode = 5
  Placement = pos=(0,4.8e-15,10.8542) rot=(1,0,0;3.14159rad)
  sketch-geometry (9):
    g0: Circle [constr] CenterX=44.0745 CenterY=2.5 CenterZ=0 NormalX=0 NormalY=0 NormalZ=1 AngleXU=0 Radius=1.4
    g1: Circle [constr] CenterX=44.0745 CenterY=2.5 CenterZ=0 NormalX=0 NormalY=0 NormalZ=1 AngleXU=0 Radius=2
    g2: ArcOfCircle CenterX=44.0745 CenterY=2.5 CenterZ=0 NormalX=0 NormalY=0 NormalZ=1 AngleXU=0 Radius=1.4 StartAngle=3.91679 EndAngle=8.64958
    g3: ArcOfCircle CenterX=44.0745 CenterY=2.5 CenterZ=0 NormalX=0 NormalY=0 NormalZ=1 AngleXU=0 Radius=2 StartAngle=4.18879 EndAngle=8.37758
    g4: LineSegment [constr] StartX=43.0745 StartY=4.23205 StartZ=0 EndX=43.0745 EndY=3.4798 EndZ=0
    g5: LineSegment [constr] StartX=43.0745 StartY=3.4798 StartZ=0 EndX=43.0745 EndY=1.5202 EndZ=0
    g6: LineSegment [constr] StartX=43.0745 StartY=1.5202 StartZ=0 EndX=43.0745 EndY=0.767949 EndZ=0
    g7: LineSegment StartX=43.0745 StartY=4.23205 StartZ=0 EndX=43.0745 EndY=3.4798 EndZ=0
    g8: LineSegment StartX=43.0745 StartY=1.5202 StartZ=0 EndX=43.0745 EndY=0.767949 EndZ=0
  constraints (22):
    c: Coincident(g0,g-3)
    c: Coincident(g1,g0)
    c: Radius(g1) = 2
    c: Radius(g0) = 1.4
    c: Tangent(g2,g0) = -1.5708
    c: PointOnObject(g2,g0)
    c: Tangent(g3,g1) = -1.5708
    c: PointOnObject(g3,g1)
    c: Coincident(g4,g3)
    c: Coincident(g4,g2)
    c: Coincident(g5,g2)
    c: Coincident(g5,g2)
    c: Coincident(g6,g2)
    c: Coincident(g6,g3)
    c: Vertical(g5)
    c: Vertical(g6)
    c: Vertical(g4)
    c: Coincident(g7,g3)
    c: Coincident(g7,g2)
    c: Coincident(g8,g2)
    c: Coincident(g8,g3)
    c: Tangent(g5,g-3)
FEATURE [PartDesign::Pocket] Pocket217
  BaseFeature = -> Pocket216
  Direction = (0,0,1)
  Length = 5
  Length2 = 5
  Placement = pos=(0,0,0) rot=(1,0,0;1.5708rad)
  Profile = -> Sketch308
  ReferenceAxis = -> Sketch308 [N_Axis]
  Refine = true
  Suppressed = false
  Type = 0
FEATURE [Sketcher::SketchObject] Sketch309
  ArcFitTolerance = 1e-06
  AttachmentSupport = -> [Pocket217]
  ExternalGeometry = -> [Pocket217]
  FullyConstrained = true
  MakeInternals = false
  MapMode = 5
  Placement = pos=(0,5.7e-15,12.8542) rot=(0,0,1;3.14159rad)
  sketch-geometry (1):
    g0: Circle CenterX=-44.0745 CenterY=2.5 CenterZ=0 NormalX=0 NormalY=0 NormalZ=1 AngleXU=0 Radius=2
  constraints (2):
    c: Coincident(g0,g-3)
    c: Equal(g0,g-3)
FEATURE [PartDesign::Pocket] Pocket218
  BaseFeature = -> Pocket217
  Direction = (0,0,-1)
  Length = 1
  Length2 = 5
  Placement = pos=(0,0,0) rot=(1,0,0;1.5708rad)
  Profile = -> Sketch309
  ReferenceAxis = -> Sketch309 [N_Axis]
  Refine = true
  Suppressed = false
  Type = 0
FEATURE [PartDesign::Body] Body029  label="Spring_Stop"
  AllowCompound = false
  Group = -> [Sketch306,Pad207,Sketch307,Pocket216,Sketch308,Pocket217,Sketch309,Pocket218]
  Origin = -> Origin031
  Placement = pos=(-0.1,40.6,0) rot=(0,0,1;0rad)
  Tip = -> Pocket218
